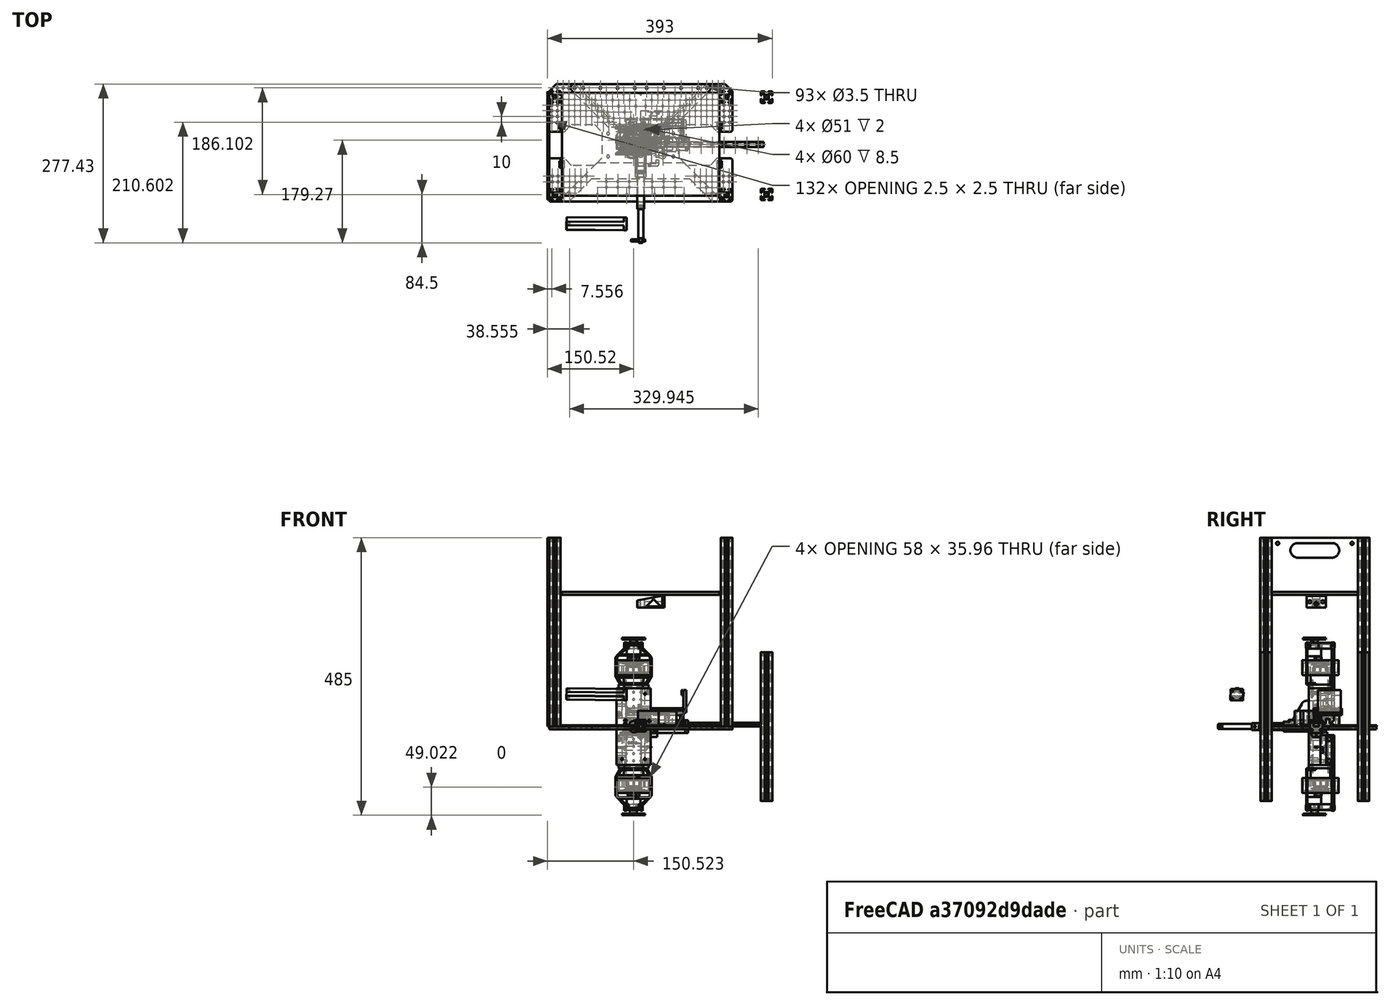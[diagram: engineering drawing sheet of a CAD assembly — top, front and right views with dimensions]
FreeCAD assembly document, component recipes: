
FREECAD ASSEMBLY — COMPONENT RECIPES ("NutSorter")

This assembly document has 31 components, labeled P0..P30 below (a component is one placed body or linked part). 29 of them carry a construction recipe — the FreeCAD feature program that regenerates the part from scratch, quoted from this document or its linked companion documents; the rest are supplied as boundary geometry only. No exploded tour is included for this assembly.
NOTE — this tour is split across 2 documents so each fits a 32k-token context. This is document 1: the component sections continue in the remaining 1 document, each repeating the header above.
COMPONENT P0 — recipe-attached ("support_pince_planche_bas", modeled in this document).
Construction recipe (the document's own serialized feature program — sketch geometry with constraints, then the solid features built on it; lengths are millimeters unless a unit is written):

FEATURE [Sketcher::SketchObject] Sketch042
  ArcFitTolerance = 1e-06
  AttachmentSupport = -> [XY_Plane019]
  FullyConstrained = true
  MakeInternals = false
  MapMode = 5
  Placement = pos=(0,0,0) rot=(0,1,0;3.14159rad)
  expr: Constraints[36] = 20 mm + VarSet.jeu
  expr: Constraints[37] = 40 mm + VarSet.jeu
  expr: Constraints[72] = 18 mm + VarSet.jeu
  expr: Constraints[73] = 20 mm + VarSet.jeu
  expr: Constraints[86] = 9 mm + VarSet.jeu
  expr: Constraints[87] = 6.5 mm + VarSet.jeu
  sketch-geometry (52):
    g0: LineSegment StartX=-28.5 StartY=-38 StartZ=0 EndX=1.8 EndY=-38 EndZ=0
    g1: LineSegment StartX=4.8 StartY=-35 StartZ=0 EndX=4.8 EndY=10 EndZ=0
    g2: ArcOfCircle CenterX=1.8 CenterY=-35 CenterZ=0 NormalX=0 NormalY=0 NormalZ=1 AngleXU=0 Radius=3 StartAngle=4.71239 EndAngle=6.28319
    g3: ArcOfCircle CenterX=1.8 CenterY=10 CenterZ=0 NormalX=0 NormalY=0 NormalZ=1 AngleXU=0 Radius=3 StartAngle=0 EndAngle=1.5708
    g4: GeomPoint [constr] X=4.8 Y=-38 Z=0
    g5: LineSegment StartX=-59.5 StartY=-13 StartZ=0 EndX=-34.5 EndY=-13 EndZ=0
    g6: LineSegment StartX=1.8 StartY=13 StartZ=0 EndX=-59.5 EndY=13 EndZ=0
    g7: ArcOfCircle CenterX=-59.5 CenterY=10 CenterZ=0 NormalX=0 NormalY=0 NormalZ=1 AngleXU=0 Radius=3 StartAngle=1.5708 EndAngle=3.14159
    g8: ArcOfCircle CenterX=-59.5 CenterY=-10 CenterZ=0 NormalX=0 NormalY=0 NormalZ=1 AngleXU=0 Radius=3 StartAngle=3.14159 EndAngle=4.71239
    g9: LineSegment StartX=-54.575 StartY=-10.075 StartZ=0 EndX=-16.425 EndY=-10.075 EndZ=0
    g10: LineSegment StartX=-15.425 StartY=-9.075 StartZ=0 EndX=-15.425 EndY=9.075 EndZ=0
    g11: LineSegment StartX=-16.425 StartY=10.075 StartZ=0 EndX=-54.575 EndY=10.075 EndZ=0
    g12: ArcOfCircle CenterX=-54.575 CenterY=9.075 CenterZ=0 NormalX=0 NormalY=0 NormalZ=1 AngleXU=0 Radius=1 StartAngle=1.5708 EndAngle=3.14159
    g13: ArcOfCircle CenterX=-54.575 CenterY=-9.075 CenterZ=0 NormalX=0 NormalY=0 NormalZ=1 AngleXU=0 Radius=1 StartAngle=3.14159 EndAngle=4.71239
    g14: ArcOfCircle CenterX=-16.425 CenterY=-9.075 CenterZ=0 NormalX=0 NormalY=0 NormalZ=1 AngleXU=0 Radius=1 StartAngle=4.71239 EndAngle=6.28319
    g15: ArcOfCircle CenterX=-16.425 CenterY=9.075 CenterZ=0 NormalX=0 NormalY=0 NormalZ=1 AngleXU=0 Radius=1 StartAngle=0 EndAngle=1.5708
    g16: GeomPoint [constr] X=-55.575 Y=10.075 Z=0
    g17: GeomPoint [constr] X=-15.425 Y=-10.075 Z=0
    g18: GeomPoint X=-35.5 Y=0 Z=0
    g19: ArcOfCircle CenterX=-34.5 CenterY=-16 CenterZ=0 NormalX=0 NormalY=0 NormalZ=1 AngleXU=0 Radius=3 StartAngle=0 EndAngle=1.5708
    g20: LineSegment StartX=-31.5 StartY=-16 StartZ=0 EndX=-31.5 EndY=-22.5 EndZ=0
    g21: ArcOfCircle CenterX=-28.5 CenterY=-35 CenterZ=0 NormalX=0 NormalY=0 NormalZ=1 AngleXU=0 Radius=3 StartAngle=3.14159 EndAngle=4.71239
    g22: GeomPoint [constr] X=-31.5 Y=-38 Z=0
    g23: GeomPoint X=-16.5 Y=-25 Z=0
    g24: LineSegment StartX=-26.575 StartY=-17.125 StartZ=0 EndX=-26.575 EndY=-22.5 EndZ=0
    g25: LineSegment StartX=-25.375 StartY=-34.075 StartZ=0 EndX=-7.625 EndY=-34.075 EndZ=0
    g26: LineSegment StartX=-6.425 StartY=-32.875 StartZ=0 EndX=-6.425 EndY=-17.125 EndZ=0
    g27: LineSegment StartX=-7.625 StartY=-15.925 StartZ=0 EndX=-25.375 EndY=-15.925 EndZ=0
    g28: ArcOfCircle CenterX=-25.375 CenterY=-17.125 CenterZ=0 NormalX=0 NormalY=0 NormalZ=1 AngleXU=0 Radius=1.2 StartAngle=1.5708 EndAngle=3.14159
    g29: ArcOfCircle CenterX=-25.375 CenterY=-32.875 CenterZ=0 NormalX=0 NormalY=0 NormalZ=1 AngleXU=0 Radius=1.2 StartAngle=3.14159 EndAngle=4.71239
    g30: ArcOfCircle CenterX=-7.625 CenterY=-32.875 CenterZ=0 NormalX=0 NormalY=0 NormalZ=1 AngleXU=0 Radius=1.2 StartAngle=4.71239 EndAngle=6.28319
    g31: ArcOfCircle CenterX=-7.625 CenterY=-17.125 CenterZ=0 NormalX=0 NormalY=0 NormalZ=1 AngleXU=0 Radius=1.2 StartAngle=-9e-16 EndAngle=1.5708
    g32: GeomPoint [constr] X=-26.575 Y=-15.925 Z=0
    g33: GeomPoint [constr] X=-6.425 Y=-34.075 Z=0
    g34: LineSegment StartX=-6.575 StartY=4.575 StartZ=0 EndX=-6.575 EndY=-4.575 EndZ=0
    g35: LineSegment StartX=-6.575 StartY=-4.575 StartZ=0 EndX=0.075 EndY=-4.575 EndZ=0
    g36: LineSegment StartX=0.075 StartY=-4.575 StartZ=0 EndX=0.075 EndY=4.575 EndZ=0
    g37: LineSegment StartX=0.075 StartY=4.575 StartZ=0 EndX=-6.575 EndY=4.575 EndZ=0
    g38: GeomPoint X=-3.25 Y=0 Z=0
    g39: LineSegment StartX=-26.575 StartY=-22.5 StartZ=0 EndX=-31.5 EndY=-22.5 EndZ=0
    g40: LineSegment StartX=-31.5 StartY=-27.5 StartZ=0 EndX=-26.575 EndY=-27.5 EndZ=0
    g41: LineSegment StartX=-26.575 StartY=-27.5 StartZ=0 EndX=-26.575 EndY=-32.875 EndZ=0
    g42: LineSegment StartX=-31.5 StartY=-27.5 StartZ=0 EndX=-31.5 EndY=-35 EndZ=0
    g43: LineSegment [constr] StartX=-16.5 StartY=-25 StartZ=0 EndX=-31.5 EndY=-25 EndZ=0
    g44: LineSegment StartX=-62.5 StartY=4 StartZ=0 EndX=-55.575 EndY=4 EndZ=0
    g45: LineSegment StartX=-62.5 StartY=-4 StartZ=0 EndX=-55.575 EndY=-4 EndZ=0
    g46: LineSegment StartX=-55.575 StartY=-4 StartZ=0 EndX=-55.575 EndY=-9.075 EndZ=0
    g47: LineSegment StartX=-62.5 StartY=-4 StartZ=0 EndX=-62.5 EndY=-10 EndZ=0
    g48: LineSegment StartX=-62.5 StartY=10 StartZ=0 EndX=-62.5 EndY=4 EndZ=0
    g49: LineSegment StartX=-55.575 StartY=9.075 StartZ=0 EndX=-55.575 EndY=4 EndZ=0
    g50: Circle CenterX=-10.5 CenterY=6 CenterZ=0 NormalX=0 NormalY=0 NormalZ=1 AngleXU=0 Radius=1.75
    g51: Circle CenterX=-10.5 CenterY=-6 CenterZ=0 NormalX=0 NormalY=0 NormalZ=1 AngleXU=0 Radius=1.75
  constraints (130):
    c: Tangent(g0,g2) = -1.5708
    c: Tangent(g1,g2) = -1.5708
    c: Tangent(g1,g3) = -1.5708
    c: Vertical(g1)
    c: Horizontal(g0)
    c: Equal(g2,g3)
    c: PointOnObject(g4,g0)
    c: PointOnObject(g4,g1)
    c: DistanceX(g-1,g1) = 4.8
    c: Tangent(g5,g8) = -1.5708
    c: Tangent(g6,g7) = -1.5708
    c: Horizontal(g5)
    c: Horizontal(g6)
    c: Equal(g7,g8)
    c: DistanceY(g5,g6) = 26
    c: Symmetric(g7,g47,g-1)
    c: Radius(g7) = 3
    c: Tangent(g3,g6) = -1.5708
    c: Tangent(g9,g13) = -1.5708
    c: Tangent(g9,g14) = -1.5708
    c: Tangent(g10,g14) = -1.5708
    c: Tangent(g10,g15) = -1.5708
    c: Tangent(g11,g15) = -1.5708
    c: Tangent(g11,g12) = -1.5708
    c: Vertical(g10)
    c: Horizontal(g9)
    c: Horizontal(g11)
    c: Equal(g12,g13)
    c: Equal(g13,g14)
    c: Equal(g14,g15)
    c: PointOnObject(g16,g11)
    c: PointOnObject(g17,g9)
    c: PointOnObject(g17,g10)
    c: Radius(g13) = 1
    c: PointOnObject(g18,g-1)
    c: Symmetric(g16,g17,g18)
    c: DistanceY(g9,g11) = 20.15
    c: DistanceX(g12,g10) = 40.15
    c: DistanceX(g18,g-1) = 35.5
    c: DistanceX(g7,g18) = 27
    c: Vertical(g20)
    c: PointOnObject(g22,g42)
    c: PointOnObject(g22,g0)
    c: Tangent(g0,g21) = -1.5708
    c: Tangent(g19,g5) = 1.5708
    c: Tangent(g20,g19) = 1.5708
    c: DistanceY(g23,g-1) = 25
    c: DistanceX(g23,g-1) = 16.5
    c: DistanceX(g19,g23) = 15
    c: DistanceY(g0,g23) = 13
    c: Equal(g21,g19)
    c: Equal(g19,g2)
    c: Equal(g3,g7)
    c: Tangent(g24,g28) = -1.5708
    c: Tangent(g25,g29) = -1.5708
    c: Tangent(g25,g30) = -1.5708
    c: Tangent(g26,g30) = -1.5708
    c: Tangent(g26,g31) = -1.5708
    c: Tangent(g27,g31) = -1.5708
    c: Tangent(g27,g28) = -1.5708
    c: Vertical(g24)
    c: Vertical(g26)
    c: Horizontal(g25)
    c: Horizontal(g27)
    c: Equal(g28,g29)
    c: Equal(g29,g30)
    c: Equal(g30,g31)
    c: PointOnObject(g32,g24)
    c: PointOnObject(g32,g27)
    c: PointOnObject(g33,g25)
    c: PointOnObject(g33,g26)
    c: Symmetric(g33,g32,g23)
    c: DistanceY(g25,g27) = 18.15
    c: DistanceX(g24,g26) = 20.15
    c: Radius(g31) = 1.2
    c: Coincident(g34,g35)
    c: Coincident(g35,g36)
    c: Coincident(g36,g37)
    c: Coincident(g37,g34)
    c: Vertical(g34)
    c: Vertical(g36)
    c: Horizontal(g35)
    c: Horizontal(g37)
    c: PointOnObject(g38,g-1)
    c: Symmetric(g36,g34,g38)
    c: DistanceX(g38,g-1) = 3.25
    c: DistanceY(g34,g34) = 9.15
    c: DistanceX(g37,g37) = 6.65
    c: Horizontal(g39)
    c: Horizontal(g40)
    c: PointOnObject(g40,g41)
    c: PointOnObject(g40,g42)
    c: Coincident(g24,g39)
    c: PointOnObject(g41,g40)
    c: Coincident(g20,g39)
    c: PointOnObject(g42,g40)
    c: Coincident(g43,g23)
    c: Horizontal(g43)
    c: Symmetric(g20,g40,g43)
    c: Vertical(g24,g40)
    c: Vertical(g40,g20)
    c: DistanceY(g40,g24) = 5
    c: Vertical(g41)
    c: Tangent(g41,g29) = -1.5708
    c: Tangent(g42,g21) = -1.5708
    c: Vertical(g42)
    c: Horizontal(g44)
    c: PointOnObject(g45,g47)
    c: Horizontal(g45)
    c: PointOnObject(g45,g46)
    c: PointOnObject(g46,g45)
    c: PointOnObject(g47,g45)
    c: Coincident(g48,g44)
    c: Vertical(g48)
    c: Tangent(g7,g48) = -1.5708
    c: Tangent(g47,g8) = -1.5708
    c: Tangent(g46,g13) = -1.5708
    c: Vertical(g46)
    c: Vertical(g47)
    c: Coincident(g49,g44)
    c: Vertical(g49)
    c: Tangent(g49,g12) = -1.5708
    c: Symmetric(g44,g45,g-1)
    c: Vertical(g16,g12)
    c: DistanceY(g45,g44) = 8
    c: Symmetric(g50,g51,g-1)
    c: DistanceX(g18,g51) = 25
    c: DistanceY(g18,g50) = 6
    c: Equal(g50,g51)
    c: Diameter(g50) = 3.5
FEATURE [PartDesign::Pad] Pad015
  Direction = (0,0,-1)
  Length = 27.5
  Length2 = 10
  Profile = -> Sketch042
  ReferenceAxis = -> Sketch042 [N_Axis]
  Reversed = true
  Suppressed = false
  Type = 0
FEATURE [Sketcher::SketchObject] Sketch055
  ArcFitTolerance = 1e-06
  AttachmentSupport = -> [XY_Plane019]
  ExternalGeometry = -> [Pad015]
  FullyConstrained = true
  MakeInternals = false
  MapMode = 5
  Placement = pos=(0,0,0) rot=(0,1,0;3.14159rad)
  sketch-geometry (8):
    g0: LineSegment StartX=-6.575 StartY=4.575 StartZ=0 EndX=-6.575 EndY=-4.575 EndZ=0
    g1: LineSegment StartX=-6.575 StartY=-4.575 StartZ=0 EndX=0.075 EndY=-4.575 EndZ=0
    g2: LineSegment StartX=0.075 StartY=-4.575 StartZ=0 EndX=0.075 EndY=4.575 EndZ=0
    g3: LineSegment StartX=0.075 StartY=4.575 StartZ=0 EndX=-6.575 EndY=4.575 EndZ=0
    g4: LineSegment StartX=-18.425 StartY=-15.925 StartZ=0 EndX=-18.425 EndY=-34.075 EndZ=0
    g5: LineSegment StartX=-18.425 StartY=-34.075 StartZ=0 EndX=-6.425 EndY=-34.075 EndZ=0
    g6: LineSegment StartX=-6.425 StartY=-34.075 StartZ=0 EndX=-6.425 EndY=-15.925 EndZ=0
    g7: LineSegment StartX=-6.425 StartY=-15.925 StartZ=0 EndX=-18.425 EndY=-15.925 EndZ=0
  constraints (22):
    c: Coincident(g0,g1)
    c: Coincident(g1,g2)
    c: Coincident(g2,g3)
    c: Coincident(g3,g0)
    c: Vertical(g0)
    c: Vertical(g2)
    c: Horizontal(g1)
    c: Horizontal(g3)
    c: Coincident(g4,g5)
    c: Coincident(g5,g6)
    c: Coincident(g6,g7)
    c: Coincident(g7,g4)
    c: Vertical(g4)
    c: Vertical(g6)
    c: Horizontal(g5)
    c: Horizontal(g7)
    c: PointOnObject(g4,g-5)
    c: PointOnObject(g6,g-6)
    c: PointOnObject(g5,g-7)
    c: DistanceX(g7,g7) = 12
    c: Coincident(g0,g-3)
    c: Coincident(g1,g-4)
FEATURE [PartDesign::Pad] Pad023
  BaseFeature = -> Pad015
  Direction = (0,0,-1)
  Length = 5
  Length2 = 10
  Profile = -> Sketch055
  ReferenceAxis = -> Sketch055 [N_Axis]
  Reversed = true
  Suppressed = false
  Type = 0
FEATURE [Sketcher::SketchObject] Sketch056
  ArcFitTolerance = 1e-06
  AttachmentOffset = pos=(0,0,-0.25) rot=(0,0,1;0rad)
  AttachmentSupport = -> [YZ_Plane019]
  ExternalGeometry = -> [Pad023]
  FullyConstrained = true
  MakeInternals = false
  MapMode = 5
  Placement = pos=(-0.25,0,0) rot=(0.57735,0.57735,0.57735;2.0944rad)
  sketch-geometry (7):
    g0: LineSegment StartX=-8.575 StartY=27.5 StartZ=0 EndX=8.575 EndY=27.5 EndZ=0
    g1: LineSegment StartX=4.575 StartY=31.5 StartZ=0 EndX=4.575 EndY=34.5 EndZ=0
    g2: LineSegment StartX=-4.575 StartY=34.5 StartZ=0 EndX=-4.575 EndY=31.5 EndZ=0
    g3: ArcOfCircle CenterX=0 CenterY=34.5 CenterZ=0 NormalX=0 NormalY=0 NormalZ=1 AngleXU=0 Radius=4.575 StartAngle=0 EndAngle=3.14159
    g4: Circle CenterX=0 CenterY=34.5 CenterZ=0 NormalX=0 NormalY=0 NormalZ=1 AngleXU=0 Radius=1.75
    g5: ArcOfCircle CenterX=-8.575 CenterY=31.5 CenterZ=0 NormalX=0 NormalY=0 NormalZ=1 AngleXU=0 Radius=4 StartAngle=4.71239 EndAngle=6.28319
    g6: ArcOfCircle CenterX=8.575 CenterY=31.5 CenterZ=0 NormalX=0 NormalY=0 NormalZ=1 AngleXU=0 Radius=4 StartAngle=3.14159 EndAngle=4.71239
  constraints (17):
    c: Vertical(g1)
    c: Vertical(g2)
    c: PointOnObject(g3,g-2)
    c: DistanceY(g-1,g3) = 34.5
    c: Tangent(g3,g1) = -1.5708
    c: Coincident(g4,g3)
    c: Diameter(g4) = 3.5
    c: Tangent(g3,g2) = -1.5708
    c: Tangent(g2,g5) = 1.5708
    c: Tangent(g0,g5) = -1.5708
    c: Horizontal(g0,g-3)
    c: Vertical(g2,g-3)
    c: Horizontal(g0,g-3)
    c: Tangent(g6,g1) = 1.5708
    c: Tangent(g0,g6) = -1.5708
    c: Equal(g1,g2)
    c: Radius(g6) = 4
FEATURE [PartDesign::Pad] Pad024
  BaseFeature = -> Pad023
  Direction = (1,0,0)
  Length = 4
  Length2 = 10
  Profile = -> Sketch056
  ReferenceAxis = -> Sketch056 [N_Axis]
  Reversed = true
  Suppressed = false
  Type = 0
FEATURE [Sketcher::SketchObject] Sketch057
  ArcFitTolerance = 1e-06
  AttachmentSupport = -> [XY_Plane019]
  ExternalGeometry = -> [Pad024]
  FullyConstrained = true
  MakeInternals = false
  MapMode = 5
  sketch-geometry (14):
    g0: ArcOfCircle CenterX=34.5 CenterY=-16 CenterZ=0 NormalX=0 NormalY=0 NormalZ=1 AngleXU=0 Radius=3 StartAngle=1.5708 EndAngle=3.14159
    g1: ArcOfCircle CenterX=39 CenterY=-20 CenterZ=0 NormalX=0 NormalY=0 NormalZ=1 AngleXU=0 Radius=5 StartAngle=4.34942 EndAngle=6.76197
    g2: LineSegment StartX=31.5 StartY=-16 StartZ=0 EndX=31.5 EndY=-22.5 EndZ=0
    g3: LineSegment StartX=34.5 StartY=-13 StartZ=0 EndX=41 EndY=-13 EndZ=0
    g4: Circle CenterX=39 CenterY=-20 CenterZ=0 NormalX=0 NormalY=0 NormalZ=1 AngleXU=0 Radius=1.75
    g5: LineSegment StartX=31.5 StartY=-22.5 StartZ=0 EndX=37.2247 EndY=-24.6742 EndZ=0
    g6: LineSegment StartX=43.4378 StartY=-17.6965 StartZ=0 EndX=41 EndY=-13 EndZ=0
    g7: Circle CenterX=29.2 CenterY=20 CenterZ=0 NormalX=0 NormalY=0 NormalZ=1 AngleXU=0 Radius=1.75
    g8: LineSegment StartX=20.2 StartY=13 StartZ=0 EndX=38.2 EndY=13 EndZ=0
    g9: LineSegment StartX=34.2 StartY=17 StartZ=0 EndX=34.2 EndY=20 EndZ=0
    g10: LineSegment StartX=24.2 StartY=17 StartZ=0 EndX=24.2 EndY=20 EndZ=0
    g11: ArcOfCircle CenterX=29.2 CenterY=20 CenterZ=0 NormalX=0 NormalY=0 NormalZ=1 AngleXU=0 Radius=5 StartAngle=0 EndAngle=3.14159
    g12: ArcOfCircle CenterX=20.2 CenterY=17 CenterZ=0 NormalX=0 NormalY=0 NormalZ=1 AngleXU=0 Radius=4 StartAngle=4.71239 EndAngle=6.28319
    g13: ArcOfCircle CenterX=38.2 CenterY=17 CenterZ=0 NormalX=0 NormalY=0 NormalZ=1 AngleXU=0 Radius=4 StartAngle=3.14159 EndAngle=4.71239
  constraints (34):
    c: Coincident(g0,g-3)
    c: Coincident(g3,g0)
    c: Horizontal(g3)
    c: Vertical(g2)
    c: Tangent(g2,g0) = -1.5708
    c: Coincident(g0,g-3)
    c: Coincident(g4,g1)
    c: Diameter(g4) = 3.5
    c: Radius(g1) = 5
    c: Coincident(g2,g5)
    c: Tangent(g5,g1) = -1.5708
    c: Coincident(g6,g3)
    c: Tangent(g6,g1) = -1.5708
    c: Equal(g3,g2)
    c: DistanceX(g3,g3) = 6.5
    c: Horizontal(g8)
    c: Vertical(g9)
    c: Vertical(g10)
    c: PointOnObject(g8,g-4)
    c: Coincident(g7,g11)
    c: Tangent(g11,g9) = -1.5708
    c: Tangent(g11,g10) = 1.5708
    c: Tangent(g10,g12) = -1.5708
    c: Tangent(g8,g12) = -1.5708
    c: Tangent(g13,g9) = 1.5708
    c: Tangent(g13,g8) = -1.5708
    c: Diameter(g7) = 3.5
    c: Equal(g11,g1)
    c: Equal(g10,g9)
    c: Radius(g13) = 4
    c: DistanceY(g-1,g7) = 20
    c: DistanceX(g-1,g7) = 29.2
    c: DistanceY(g1,g-1) = 20
    c: DistanceX(g-1,g1) = 39
FEATURE [PartDesign::Pad] Pad025
  BaseFeature = -> Pad024
  Direction = (0,0,1)
  Length = 3
  Length2 = 10
  Profile = -> Sketch057
  ReferenceAxis = -> Sketch057 [N_Axis]
  Suppressed = false
  Type = 0
FEATURE [Sketcher::SketchObject] Sketch058
  ArcFitTolerance = 1e-06
  AttachmentOffset = pos=(15,9.6,25) rot=(0,0,1;0rad)
  AttachmentSupport = -> [XZ_Plane019]
  FullyConstrained = true
  MakeInternals = false
  MapMode = 5
  Placement = pos=(15,-25,9.6) rot=(1,0,0;1.5708rad)
  sketch-geometry (2):
    g0: ArcOfCircle CenterX=0 CenterY=0 CenterZ=0 NormalX=0 NormalY=0 NormalZ=1 AngleXU=0 Radius=2.25 StartAngle=1.99427 EndAngle=7.43051
    g1: ArcOfCircle CenterX=0 CenterY=1 CenterZ=0 NormalX=0 NormalY=0 NormalZ=1 AngleXU=0 Radius=1.4 StartAngle=0.849413 EndAngle=2.29218
  constraints (7):
    c: Coincident(g0,g-1)
    c: Diameter(g0) = 4.5
    c: Coincident(g1,g0)
    c: Coincident(g1,g0)
    c: PointOnObject(g1,g-2)
    c: DistanceY(g0,g1) = 1
    c: Radius(g1) = 1.4
FEATURE [PartDesign::Pocket] Pocket028
  BaseFeature = -> Pad025
  Direction = (0,1,-2e-16)
  Length = 27
  Length2 = 5
  Midplane = true
  Profile = -> Sketch058
  ReferenceAxis = -> Sketch058 [N_Axis]
  Suppressed = false
  Type = 0
FEATURE [Sketcher::SketchObject] Sketch059
  ArcFitTolerance = 1e-06
  AttachmentSupport = -> [Pocket028]
  ExternalGeometry = -> [Pocket028]
  FullyConstrained = true
  MakeInternals = false
  MapMode = 5
  Placement = pos=(0,0,27.5) rot=(0,0,1;0rad)
  sketch-geometry (2):
    g0: Circle CenterX=10.5 CenterY=6 CenterZ=0 NormalX=0 NormalY=0 NormalZ=1 AngleXU=0 Radius=2.1
    g1: Circle CenterX=10.5 CenterY=-6 CenterZ=0 NormalX=0 NormalY=0 NormalZ=1 AngleXU=0 Radius=2.1
  constraints (4):
    c: Coincident(g0,g-3)
    c: Coincident(g1,g-4)
    c: Equal(g0,g1)
    c: Diameter(g0) = 4.2
FEATURE [PartDesign::Pocket] Pocket029
  BaseFeature = -> Pocket028
  Direction = (0,0,-1)
  Length = 1.5
  Length2 = 5
  Profile = -> Sketch059
  ReferenceAxis = -> Sketch059 [N_Axis]
  Suppressed = false
  Type = 0
FEATURE [PartDesign::Fillet] Fillet
  Base = -> Pocket029 [Edge169,Edge108]
  BaseFeature = -> Pocket029
  Radius = 3
  SupportTransform = false
  Suppressed = false
  UseAllEdges = false
FEATURE [PartDesign::Body] Body013  label="support_pince_planche_bas"
  AllowCompound = false
  Group = -> [Sketch042,Pad015,Sketch055,Pad023,Sketch056,Pad024,Sketch057,Pad025,Sketch058,Pocket028,Sketch059,Pocket029,Fillet]
  Origin = -> Origin019
  Tip = -> Fillet
COMPONENT P1 — recipe-attached ("support_pince_planche_haut", modeled in this document).
Construction recipe (the document's own serialized feature program — sketch geometry with constraints, then the solid features built on it; lengths are millimeters unless a unit is written):

FEATURE [Sketcher::SketchObject] Sketch063
  ArcFitTolerance = 1e-06
  AttachmentSupport = -> [XY_Plane024]
  FullyConstrained = true
  MakeInternals = false
  MapMode = 5
  sketch-geometry (11):
    g0: LineSegment StartX=-3.15 StartY=4.65 StartZ=0 EndX=-3.15 EndY=-4.65 EndZ=0
    g1: LineSegment StartX=-3.15 StartY=-4.65 StartZ=0 EndX=3.15 EndY=-4.65 EndZ=0
    g2: LineSegment StartX=3.15 StartY=-4.65 StartZ=0 EndX=3.15 EndY=4.65 EndZ=0
    g3: LineSegment StartX=3.15 StartY=4.65 StartZ=0 EndX=-3.15 EndY=4.65 EndZ=0
    g4: LineSegment StartX=-6.15 StartY=4.65 StartZ=0 EndX=-6.15 EndY=-4.65 EndZ=0
    g5: LineSegment StartX=-3.15 StartY=-7.65 StartZ=0 EndX=38.5 EndY=-7.65 EndZ=0
    g6: LineSegment StartX=38.5 StartY=-7.65 StartZ=0 EndX=38.5 EndY=7.65 EndZ=0
    g7: LineSegment StartX=38.5 StartY=7.65 StartZ=0 EndX=-3.15 EndY=7.65 EndZ=0
    g8: ArcOfCircle CenterX=-3.15 CenterY=4.65 CenterZ=0 NormalX=0 NormalY=0 NormalZ=1 AngleXU=0 Radius=3 StartAngle=1.5708 EndAngle=3.14159
    g9: ArcOfCircle CenterX=-3.15 CenterY=-4.65 CenterZ=0 NormalX=0 NormalY=0 NormalZ=1 AngleXU=0 Radius=3 StartAngle=3.14159 EndAngle=4.71239
    g10: GeomPoint [constr] X=-6.15 Y=7.65 Z=0
  constraints (27):
    c: Coincident(g0,g1)
    c: Coincident(g1,g2)
    c: Coincident(g2,g3)
    c: Coincident(g3,g0)
    c: Vertical(g0)
    c: Vertical(g2)
    c: Horizontal(g1)
    c: Horizontal(g3)
    c: Tangent(g4,g8) = -1.5708
    c: Tangent(g4,g9) = -1.5708
    c: Tangent(g5,g9) = -1.5708
    c: Tangent(g7,g8) = -1.5708
    c: Vertical(g4)
    c: Horizontal(g5)
    c: Horizontal(g7)
    c: Equal(g8,g9)
    c: PointOnObject(g10,g4)
    c: PointOnObject(g10,g7)
    c: Radius(g9) = 3
    c: Coincident(g6,g7)
    c: Coincident(g5,g6)
    c: Symmetric(g6,g5,g-1)
    c: Symmetric(g2,g0,g-1)
    c: DistanceY(g0,g0) = 9.3
    c: DistanceX(g3,g3) = 6.3
    c: Coincident(g0,g8)
    c: DistanceX(g-1,g6) = 38.5
FEATURE [PartDesign::Pad] Pad029
  Direction = (0,0,1)
  Length = 5
  Length2 = 10
  Profile = -> Sketch063
  ReferenceAxis = -> Sketch063 [N_Axis]
  Suppressed = false
  Type = 0
FEATURE [Sketcher::SketchObject] Sketch064
  ArcFitTolerance = 1e-06
  AttachmentSupport = -> [Pad029]
  ExternalGeometry = -> [Pad029]
  FullyConstrained = true
  MakeInternals = false
  MapMode = 5
  Placement = pos=(38.5,0,0) rot=(0.57735,0.57735,0.57735;2.0944rad)
  sketch-geometry (8):
    g0: Circle CenterX=0 CenterY=16 CenterZ=0 NormalX=0 NormalY=0 NormalZ=1 AngleXU=0 Radius=2.75
    g1: LineSegment StartX=-7.65 StartY=19 StartZ=0 EndX=-7.65 EndY=5 EndZ=0
    g2: LineSegment StartX=7.65 StartY=5 StartZ=0 EndX=7.65 EndY=19 EndZ=0
    g3: LineSegment StartX=4.65 StartY=22 StartZ=0 EndX=-4.65 EndY=22 EndZ=0
    g4: ArcOfCircle CenterX=-4.65 CenterY=19 CenterZ=0 NormalX=0 NormalY=0 NormalZ=1 AngleXU=0 Radius=3 StartAngle=1.5708 EndAngle=3.14159
    g5: ArcOfCircle CenterX=4.65 CenterY=19 CenterZ=0 NormalX=0 NormalY=0 NormalZ=1 AngleXU=0 Radius=3 StartAngle=-9e-16 EndAngle=1.5708
    g6: GeomPoint [constr] X=-7.65 Y=22 Z=0
    g7: LineSegment StartX=-7.65 StartY=5 StartZ=0 EndX=7.65 EndY=5 EndZ=0
  constraints (19):
    c: Diameter(g0) = 5.5
    c: PointOnObject(g0,g-2)
    c: Tangent(g1,g4) = -1.5708
    c: Tangent(g2,g5) = -1.5708
    c: Tangent(g3,g5) = -1.5708
    c: Tangent(g3,g4) = -1.5708
    c: Vertical(g1)
    c: Vertical(g2)
    c: Horizontal(g3)
    c: PointOnObject(g6,g1)
    c: PointOnObject(g6,g3)
    c: Coincident(g1,g-3)
    c: Coincident(g2,g-3)
    c: Equal(g5,g4)
    c: Radius(g4) = 3
    c: DistanceY(g2,g0) = 11
    c: Coincident(g7,g1)
    c: Coincident(g7,g2)
    c: DistanceY(g0,g3) = 6
FEATURE [PartDesign::Pad] Pad030
  BaseFeature = -> Pad029
  Direction = (1,0,0)
  Length = 3
  Length2 = 10
  Profile = -> Sketch064
  ReferenceAxis = -> Sketch064 [N_Axis]
  Reversed = true
  Suppressed = false
  Type = 0
FEATURE [PartDesign::Chamfer] Chamfer  label="Chamfer001"
  Angle = 45
  Base = -> Pad030 [Edge19]
  BaseFeature = -> Pad030
  ChamferType = 1
  FlipDirection = false
  Size = 15
  Size2 = 5
  SupportTransform = false
  Suppressed = false
  UseAllEdges = false
FEATURE [PartDesign::Body] Body017  label="support_pince_planche_haut"
  AllowCompound = false
  Group = -> [Sketch063,Pad029,Sketch064,Pad030,Chamfer]
  Origin = -> Origin024
  Placement = pos=(3,-2.563e-05,214) rot=(0,0,1;0rad)
  Tip = -> Chamfer
COMPONENT P2 — recipe-attached ("pince_capot001", modeled in this document).
Construction recipe (the document's own serialized feature program — sketch geometry with constraints, then the solid features built on it; lengths are millimeters unless a unit is written):

FEATURE [Sketcher::SketchObject] Sketch242
  ArcFitTolerance = 0
  AttachmentSupport = -> [XY_Plane281]
  FullyConstrained = true
  MakeInternals = false
  MapMode = 2
  sketch-geometry (31):
    g0: LineSegment StartX=0 StartY=50 StartZ=0 EndX=100 EndY=50 EndZ=0
    g1: LineSegment StartX=100 StartY=50 StartZ=0 EndX=100 EndY=48 EndZ=0
    g2: LineSegment StartX=100 StartY=0 StartZ=0 EndX=0 EndY=0 EndZ=0
    g3: LineSegment StartX=0 StartY=0 StartZ=0 EndX=0 EndY=2 EndZ=0
    g4: Circle CenterX=50 CenterY=25 CenterZ=0 NormalX=0 NormalY=0 NormalZ=1 AngleXU=0 Radius=14
    g5: LineSegment [constr] StartX=0 StartY=50 StartZ=0 EndX=100 EndY=0 EndZ=0
    g6: LineSegment [constr] StartX=0 StartY=0 StartZ=0 EndX=100 EndY=50 EndZ=0
    g7: LineSegment [constr] StartX=0 StartY=25 StartZ=0 EndX=100 EndY=25 EndZ=0
    g8: LineSegment [constr] StartX=50 StartY=50 StartZ=0 EndX=50 EndY=0 EndZ=0
    g9: LineSegment [constr] StartX=3.5 StartY=33.25 StartZ=0 EndX=96.5 EndY=33.25 EndZ=0
    g10: LineSegment [constr] StartX=96.5 StartY=33.25 StartZ=0 EndX=96.5 EndY=16.75 EndZ=0
    g11: LineSegment [constr] StartX=96.5 StartY=16.75 StartZ=0 EndX=3.5 EndY=16.75 EndZ=0
    g12: LineSegment [constr] StartX=3.5 StartY=16.75 StartZ=0 EndX=3.5 EndY=33.25 EndZ=0
    g13: Circle CenterX=96.5 CenterY=33.25 CenterZ=0 NormalX=0 NormalY=0 NormalZ=1 AngleXU=0 Radius=1.65
    g14: Circle CenterX=3.5 CenterY=33.25 CenterZ=0 NormalX=0 NormalY=0 NormalZ=1 AngleXU=0 Radius=1.65
    g15: Circle CenterX=3.5 CenterY=16.75 CenterZ=0 NormalX=0 NormalY=0 NormalZ=1 AngleXU=0 Radius=1.65
    g16: Circle CenterX=96.5 CenterY=16.75 CenterZ=0 NormalX=0 NormalY=0 NormalZ=1 AngleXU=0 Radius=1.65
    g17: LineSegment StartX=0 StartY=2 StartZ=0 EndX=30 EndY=2 EndZ=0
    g18: LineSegment StartX=30 StartY=2 StartZ=0 EndX=30 EndY=7.5 EndZ=0
    g19: LineSegment StartX=30 StartY=7.5 StartZ=0 EndX=2.5 EndY=7.5 EndZ=0
    g20: LineSegment StartX=0 StartY=10 StartZ=0 EndX=0 EndY=50 EndZ=0
    g21: LineSegment StartX=100 StartY=48 StartZ=0 EndX=67.5 EndY=48 EndZ=0
    g22: LineSegment StartX=67.5 StartY=48 StartZ=0 EndX=67.5 EndY=42.5 EndZ=0
    g23: LineSegment StartX=67.5 StartY=42.5 StartZ=0 EndX=97.5 EndY=42.5 EndZ=0
    g24: LineSegment StartX=100 StartY=40 StartZ=0 EndX=100 EndY=0 EndZ=0
    g25: ArcOfCircle [constr] CenterX=97.5 CenterY=40 CenterZ=0 NormalX=0 NormalY=0 NormalZ=1 AngleXU=0 Radius=2.5 StartAngle=0 EndAngle=1.5708
    g26: GeomPoint [constr] X=100 Y=42.5 Z=0
    g27: LineSegment StartX=100 StartY=40 StartZ=0 EndX=97.5 EndY=42.5 EndZ=0
    g28: ArcOfCircle [constr] CenterX=2.5 CenterY=10 CenterZ=0 NormalX=0 NormalY=0 NormalZ=1 AngleXU=0 Radius=2.5 StartAngle=3.14159 EndAngle=4.71239
    g29: GeomPoint [constr] X=0 Y=7.5 Z=0
    g30: LineSegment StartX=0 StartY=10 StartZ=0 EndX=2.5 EndY=7.5 EndZ=0
  constraints (78):
    c: Coincident(g0,g1)
    c: Coincident(g24,g2)
    c: Coincident(g2,g3)
    c: Coincident(g20,g0)
    c: Horizontal(g0)
    c: Horizontal(g2)
    c: Vertical(g1)
    c: Vertical(g3)
    c: Coincident(g2,g-1)
    c: Coincident(g5,g0)
    c: Coincident(g2,g6)
    c: Coincident(g0,g6)
    c: Coincident(g24,g5)
    c: PointOnObject(g4,g6)
    c: PointOnObject(g4,g5)
    c: Diameter(g4) = 28
    c: DistanceY(g3,g20) = 50
    c: DistanceX(g2,g2) = 100
    c: PointOnObject(g8,g0)
    c: PointOnObject(g7,g24)
    c: PointOnObject(g7,g20)
    c: PointOnObject(g8,g2)
    c: Symmetric(g0,g0,g8)
    c: Symmetric(g0,g2,g7)
    c: Coincident(g9,g10)
    c: Coincident(g10,g11)
    c: Coincident(g11,g12)
    c: Coincident(g12,g9)
    c: Horizontal(g11)
    c: Vertical(g12)
    c: Symmetric(g9,g10,g7)
    c: Symmetric(g9,g9,g8)
    c: Distance(g12) = 16.5
    c: DistanceX(g0,g9) = 3.5
    c: Coincident(g16,g10)
    c: Coincident(g13,g9)
    c: Coincident(g9,g14)
    c: Coincident(g11,g15)
    c: Equal(g14,g15)
    c: Equal(g14,g13)
    c: Equal(g14,g16)
    c: Diameter(g14) = 3.3
    c: Coincident(g17,g18)
    c: Coincident(g18,g19)
    c: Horizontal(g17)
    c: Horizontal(g19)
    c: Vertical(g18)
    c: Vertical(g20)
    c: DistanceX(g29,g19) = 30
    c: Coincident(g21,g22)
    c: Coincident(g22,g23)
    c: Horizontal(g21)
    c: Horizontal(g23)
    c: Vertical(g22)
    c: Vertical(g24)
    c: Equal(g18,g22)
    c: PointOnObject(g26,g23)
    c: PointOnObject(g26,g24)
    c: Tangent(g23,g25) = 1.5708
    c: Tangent(g24,g25) = 1.5708
    c: Coincident(g27,g23)
    c: Coincident(g27,g24)
    c: PointOnObject(g29,g20)
    c: PointOnObject(g29,g19)
    c: Tangent(g20,g28) = 1.5708
    c: Tangent(g19,g28) = 1.5708
    c: Coincident(g30,g20)
    c: Coincident(g30,g19)
    c: Equal(g1,g3)
    c: Equal(g23,g17)
    c: Coincident(g3,g17)
    c: DistanceY(g3,g3) = 2
    c: Coincident(g1,g21)
    c: Vertical(g1,g24)
    c: Vertical(g29,g3)
    c: DistanceY(g18,g18) = 5.5
    c: Radius(g28) = 2.5
    c: Equal(g25,g28)
FEATURE [PartDesign::Pad] Pad118
  AlongSketchNormal = false
  Direction = (0,0,1)
  Length = 4
  Length2 = 100
  Profile = -> Sketch242
  ReferenceAxis = -> Sketch242 [N_Axis]
  Suppressed = false
  Type = 0
FEATURE [Sketcher::SketchObject] Sketch243
  ArcFitTolerance = 1e-06
  AttachmentOffset = pos=(0,0,4) rot=(0,0,1;0rad)
  AttachmentSupport = -> [XY_Plane281]
  ExternalGeometry = -> [Pad118]
  FullyConstrained = true
  MakeInternals = false
  MapMode = 5
  Placement = pos=(0,0,4) rot=(0,0,1;0rad)
  sketch-geometry (4):
    g0: Circle CenterX=3.5 CenterY=33.25 CenterZ=0 NormalX=0 NormalY=0 NormalZ=1 AngleXU=0 Radius=3.25
    g1: Circle CenterX=3.5 CenterY=16.75 CenterZ=0 NormalX=0 NormalY=0 NormalZ=1 AngleXU=0 Radius=3.25
    g2: Circle CenterX=96.5 CenterY=33.25 CenterZ=0 NormalX=0 NormalY=0 NormalZ=1 AngleXU=0 Radius=3.25
    g3: Circle CenterX=96.5 CenterY=16.75 CenterZ=0 NormalX=0 NormalY=0 NormalZ=1 AngleXU=0 Radius=3.25
  constraints (10):
    c: Coincident(g0,g-3)
    c: Coincident(g1,g-4)
    c: Equal(g0,g1)
    c: Equal(g1,g2)
    c: Equal(g2,g3)
    c: Diameter(g0) = 6.5
    c: Horizontal(g3,g1)
    c: Horizontal(g2,g0)
    c: Vertical(g2,g3)
    c: DistanceX(g1,g3) = 93
FEATURE [PartDesign::Pocket] Pocket099
  BaseFeature = -> Pad118
  Direction = (0,0,-1)
  Length = 2
  Length2 = 5
  Profile = -> Sketch243
  ReferenceAxis = -> Sketch243 [N_Axis]
  Refine = true
  Suppressed = false
  Type = 0
FEATURE [PartDesign::Body] Body083  label="pince_capot001"
  AllowCompound = false
  Group = -> [Sketch242,Pad118,Sketch243,Pocket099]
  Origin = -> Origin284
  Placement = pos=(-25,-5,28) rot=(0,0,1;0rad)
  Tip = -> Pocket099
COMPONENT P3 — recipe-attached ("pince_cremaillere_bras002", modeled in this document).
Construction recipe (the document's own serialized feature program — sketch geometry with constraints, then the solid features built on it; lengths are millimeters unless a unit is written):

FEATURE [PartDesign::FeatureBase] BaseFeature002
  BaseFeature = -> InvoluteRack001
  Suppressed = false
FEATURE [Sketcher::SketchObject] Sketch244
  ArcFitTolerance = 1e-06
  AttachmentSupport = -> [BaseFeature002]
  FullyConstrained = true
  MakeInternals = false
  MapMode = 5
  Placement = pos=(0,92.677,0) rot=(0,0.707107,0.707107;3.14159rad)
  sketch-geometry (4):
    g0: LineSegment StartX=-29.25 StartY=0 StartZ=0 EndX=10.75 EndY=0 EndZ=0
    g1: LineSegment StartX=10.75 StartY=0 StartZ=0 EndX=10.75 EndY=40 EndZ=0
    g2: LineSegment StartX=10.75 StartY=40 StartZ=0 EndX=-29.25 EndY=40 EndZ=0
    g3: LineSegment StartX=-29.25 StartY=40 StartZ=0 EndX=-29.25 EndY=0 EndZ=0
  constraints (12):
    c: Coincident(g0,g1)
    c: Coincident(g1,g2)
    c: Coincident(g2,g3)
    c: Coincident(g3,g0)
    c: Horizontal(g0)
    c: Horizontal(g2)
    c: Vertical(g1)
    c: Vertical(g3)
    c: DistanceY(g3,g3) = 40
    c: DistanceX(g2,g2) = 40
    c: PointOnObject(g0,g-1)
    c: DistanceX(g-1,g0) = 10.75
FEATURE [PartDesign::Pad] Pad119
  BaseFeature = -> BaseFeature002
  Direction = (0,1,-2e-16)
  Length = 5
  Length2 = 10
  Profile = -> Sketch244
  ReferenceAxis = -> Sketch244 [N_Axis]
  Refine = true
  Suppressed = false
  Type = 0
FEATURE [Sketcher::SketchObject] Sketch262
  ArcFitTolerance = 1e-06
  AttachmentOffset = pos=(0,0,-10.75) rot=(0,0,1;0rad)
  AttachmentSupport = -> [YZ_Plane282]
  ExternalGeometry = -> [Pad119]
  FullyConstrained = true
  MakeInternals = false
  MapMode = 5
  Placement = pos=(-10.75,0,0) rot=(0.57735,0.57735,0.57735;2.0944rad)
  sketch-geometry (3):
    g0: LineSegment StartX=67.677 StartY=3 StartZ=0 EndX=92.677 EndY=9 EndZ=0
    g1: LineSegment StartX=67.677 StartY=3 StartZ=0 EndX=92.677 EndY=3 EndZ=0
    g2: LineSegment StartX=92.677 StartY=9 StartZ=0 EndX=92.677 EndY=3 EndZ=0
  constraints (8):
    c: PointOnObject(g0,g-4)
    c: Coincident(g1,g0)
    c: Coincident(g1,g-4)
    c: Coincident(g2,g0)
    c: Coincident(g2,g1)
    c: DistanceX(g1,g1) = 25
    c: Vertical(g2)
    c: DistanceY(g2,g2) = 6
FEATURE [PartDesign::Pad] Pad124
  BaseFeature = -> Pad119
  Direction = (1,0,0)
  Length = 5
  Length2 = 10
  Profile = -> Sketch262
  ReferenceAxis = -> Sketch262 [N_Axis]
  Suppressed = false
  Type = 0
FEATURE [PartDesign::Body] Body084  label="pince_cremaillere_bras002"
  AllowCompound = false
  BaseFeature = -> InvoluteRack001
  Group = -> [BaseFeature002,Sketch244,Pad119,Sketch262,Pad124]
  Origin = -> Origin285
  Placement = pos=(-18.1714,32.25,24) rot=(0,0,-1;1.5708rad)
  Tip = -> Pad124
COMPONENT P4 — recipe-attached ("pince_support_servo001", modeled in this document).
Construction recipe (the document's own serialized feature program — sketch geometry with constraints, then the solid features built on it; lengths are millimeters unless a unit is written):

FEATURE [Sketcher::SketchObject] Sketch245
  ArcFitTolerance = 0
  AttachmentOffset = pos=(0,0,-2) rot=(0,0,1;0rad)
  AttachmentSupport = -> [XY_Plane283]
  FullyConstrained = true
  MakeInternals = false
  MapMode = 2
  Placement = pos=(0,0,-2) rot=(0,0,1;0rad)
  sketch-geometry (18):
    g0: LineSegment StartX=14.5 StartY=50 StartZ=0 EndX=35.5 EndY=50 EndZ=0
    g1: LineSegment StartX=35.5 StartY=50 StartZ=0 EndX=35.5 EndY=9 EndZ=0
    g2: LineSegment StartX=35.5 StartY=9 StartZ=0 EndX=14.5 EndY=9 EndZ=0
    g3: LineSegment StartX=14.5 StartY=9 StartZ=0 EndX=14.5 EndY=50 EndZ=0
    g4: LineSegment StartX=0 StartY=59 StartZ=0 EndX=50 EndY=59 EndZ=0
    g5: LineSegment StartX=50 StartY=59 StartZ=0 EndX=50 EndY=0 EndZ=0
    g6: LineSegment StartX=50 StartY=0 StartZ=0 EndX=0 EndY=0 EndZ=0
    g7: LineSegment StartX=0 StartY=0 StartZ=0 EndX=0 EndY=59 EndZ=0
    g8: Circle CenterX=19 CenterY=54.5 CenterZ=0 NormalX=0 NormalY=0 NormalZ=1 AngleXU=0 Radius=1.65
    g9: Circle CenterX=31 CenterY=54.5 CenterZ=0 NormalX=0 NormalY=0 NormalZ=1 AngleXU=0 Radius=1.65
    g10: Circle CenterX=19 CenterY=4.5 CenterZ=0 NormalX=0 NormalY=0 NormalZ=1 AngleXU=0 Radius=1.65
    g11: Circle CenterX=31 CenterY=4.5 CenterZ=0 NormalX=0 NormalY=0 NormalZ=1 AngleXU=0 Radius=1.65
    g12: LineSegment [constr] StartX=19 StartY=54.5 StartZ=0 EndX=31 EndY=54.5 EndZ=0
    g13: LineSegment [constr] StartX=31 StartY=54.5 StartZ=0 EndX=31 EndY=4.5 EndZ=0
    g14: LineSegment [constr] StartX=31 StartY=4.5 StartZ=0 EndX=19 EndY=4.5 EndZ=0
    g15: LineSegment [constr] StartX=19 StartY=4.5 StartZ=0 EndX=19 EndY=54.5 EndZ=0
    g16: LineSegment [constr] StartX=14.5 StartY=29.5 StartZ=0 EndX=35.5 EndY=29.5 EndZ=0
    g17: LineSegment [constr] StartX=25 StartY=50 StartZ=0 EndX=25 EndY=9 EndZ=0
  constraints (46):
    c: Coincident(g0,g1)
    c: Coincident(g1,g2)
    c: Coincident(g2,g3)
    c: Coincident(g3,g0)
    c: Horizontal(g0)
    c: Horizontal(g2)
    c: Vertical(g1)
    c: Vertical(g3)
    c: Coincident(g4,g5)
    c: Coincident(g5,g6)
    c: Coincident(g6,g7)
    c: Coincident(g7,g4)
    c: Horizontal(g6)
    c: Vertical(g5)
    c: Coincident(g12,g13)
    c: Coincident(g13,g14)
    c: Coincident(g14,g15)
    c: Coincident(g15,g12)
    c: Horizontal(g14)
    c: Vertical(g15)
    c: Coincident(g10,g14)
    c: Coincident(g11,g13)
    c: Coincident(g8,g12)
    c: Coincident(g9,g12)
    c: PointOnObject(g17,g0)
    c: PointOnObject(g17,g2)
    c: PointOnObject(g16,g3)
    c: PointOnObject(g16,g1)
    c: Symmetric(g0,g0,g17)
    c: Symmetric(g2,g0,g16)
    c: Symmetric(g9,g8,g17)
    c: DistanceX(g2,g2) = 21
    c: DistanceY(g3,g3) = 41
    c: DistanceX(g14,g14) = 12
    c: DistanceY(g13,g13) = 50
    c: Equal(g9,g8)
    c: Equal(g9,g11)
    c: Equal(g9,g10)
    c: Diameter(g9) = 3.3
    c: Symmetric(g9,g11,g16)
    c: Coincident(g-1,g6)
    c: Symmetric(g4,g4,g17)
    c: DistanceX(g6,g2) = 14.5
    c: Vertical(g7)
    c: DistanceY(g5,g5) = 59
    c: DistanceY(g-1,g2) = 9
FEATURE [PartDesign::Pad] Pad120
  AlongSketchNormal = false
  Direction = (0,0,1)
  Length = 4
  Length2 = 100
  Profile = -> Sketch245
  ReferenceAxis = -> Sketch245 [N_Axis]
  Suppressed = false
  Type = 0
FEATURE [Sketcher::SketchObject] Sketch246
  ArcFitTolerance = 0
  AttachmentSupport = -> [Pad120]
  ExternalGeometry = -> [Pad120]
  FullyConstrained = true
  MakeInternals = false
  MapMode = 5
  Placement = pos=(0,0,2) rot=(0,0,1;0rad)
  sketch-geometry (10):
    g0: LineSegment StartX=0 StartY=40 StartZ=0 EndX=8 EndY=40 EndZ=0
    g1: LineSegment StartX=8 StartY=40 StartZ=0 EndX=8 EndY=0 EndZ=0
    g2: LineSegment StartX=8 StartY=0 StartZ=0 EndX=0 EndY=0 EndZ=0
    g3: LineSegment StartX=0 StartY=0 StartZ=0 EndX=0 EndY=40 EndZ=0
    g4: LineSegment StartX=42 StartY=40 StartZ=0 EndX=50 EndY=40 EndZ=0
    g5: LineSegment StartX=50 StartY=40 StartZ=0 EndX=50 EndY=0 EndZ=0
    g6: LineSegment StartX=50 StartY=0 StartZ=0 EndX=42 EndY=0 EndZ=0
    g7: LineSegment StartX=42 StartY=0 StartZ=0 EndX=42 EndY=40 EndZ=0
    g8: LineSegment [constr] StartX=25 StartY=59 StartZ=0 EndX=25 EndY=0 EndZ=0
    g9: LineSegment [constr] StartX=0 StartY=20 StartZ=0 EndX=50 EndY=20 EndZ=0
  constraints (28):
    c: Coincident(g0,g1)
    c: Coincident(g1,g2)
    c: Coincident(g2,g3)
    c: Coincident(g3,g0)
    c: Horizontal(g0)
    c: Horizontal(g2)
    c: Vertical(g3)
    c: Coincident(g4,g5)
    c: Coincident(g5,g6)
    c: Coincident(g6,g7)
    c: Coincident(g7,g4)
    c: Horizontal(g4)
    c: Horizontal(g6)
    c: Vertical(g5)
    c: PointOnObject(g4,g-4)
    c: PointOnObject(g8,g-5)
    c: PointOnObject(g8,g-6)
    c: Symmetric(g-5,g-5,g8)
    c: Symmetric(g0,g4,g8)
    c: DistanceX(g0,g0) = 8
    c: Vertical(g1)
    c: PointOnObject(g9,g3)
    c: PointOnObject(g9,g5)
    c: Symmetric(g0,g1,g9)
    c: Vertical(g7)
    c: PointOnObject(g5,g-1)
    c: DistanceY(g3,g3) = 40
    c: Coincident(g2,g-1)
FEATURE [PartDesign::Pad] Pad121
  AlongSketchNormal = false
  BaseFeature = -> Pad120
  Direction = (0,0,1)
  Length = 18
  Length2 = 100
  Profile = -> Sketch246
  Suppressed = false
  Type = 0
FEATURE [Sketcher::SketchObject] Sketch247
  ArcFitTolerance = 0
  AttachmentSupport = -> [Pad121]
  ExternalGeometry = -> [Pad121]
  FullyConstrained = true
  MakeInternals = false
  MapMode = 5
  Placement = pos=(0,0,20) rot=(0,0,1;0rad)
  sketch-geometry (7):
    g0: LineSegment [constr] StartX=25 StartY=40 StartZ=0 EndX=25 EndY=0 EndZ=0
    g1: LineSegment [constr] StartX=0 StartY=20 StartZ=0 EndX=50 EndY=20 EndZ=0
    g2: Circle CenterX=4 CenterY=36 CenterZ=0 NormalX=0 NormalY=0 NormalZ=1 AngleXU=0 Radius=1.75
    g3: Circle CenterX=46 CenterY=36 CenterZ=0 NormalX=0 NormalY=0 NormalZ=1 AngleXU=0 Radius=1.75
    g4: Circle CenterX=4 CenterY=4 CenterZ=0 NormalX=0 NormalY=0 NormalZ=1 AngleXU=0 Radius=1.75
    g5: Circle CenterX=46 CenterY=4 CenterZ=0 NormalX=0 NormalY=0 NormalZ=1 AngleXU=0 Radius=1.75
    g6: LineSegment [constr] StartX=4 StartY=36 StartZ=0 EndX=4 EndY=4 EndZ=0
  constraints (17):
    c: PointOnObject(g0,g-4)
    c: PointOnObject(g0,g-5)
    c: PointOnObject(g1,g-7)
    c: PointOnObject(g1,g-8)
    c: Symmetric(g-3,g-4,g0)
    c: Symmetric(g-5,g-4,g1)
    c: Symmetric(g4,g2,g1)
    c: Symmetric(g3,g2,g0)
    c: Symmetric(g5,g3,g1)
    c: Equal(g2,g4)
    c: Equal(g2,g3)
    c: Equal(g2,g5)
    c: Radius(g2) = 1.75
    c: Coincident(g6,g4)
    c: Coincident(g6,g2)
    c: Symmetric(g-7,g-5,g6)
    c: DistanceY(g-5,g4) = 4
FEATURE [PartDesign::Pocket] Pocket100
  BaseFeature = -> Pad121
  Direction = (0,0,-1)
  Length = 5
  Length2 = 100
  Profile = -> Sketch247
  Suppressed = false
  Type = 1
FEATURE [Sketcher::SketchObject] Sketch248
  ArcFitTolerance = 0
  AttachmentSupport = -> [Pocket100]
  ExternalGeometry = -> [Pocket100]
  FullyConstrained = true
  MakeInternals = false
  MapMode = 5
  Placement = pos=(50,0,0) rot=(0.57735,0.57735,0.57735;2.0944rad)
  sketch-geometry (7):
    g0: LineSegment [constr] StartX=0 StartY=20 StartZ=0 EndX=40 EndY=0 EndZ=0
    g1: LineSegment [constr] StartX=0 StartY=0 StartZ=0 EndX=40 EndY=20 EndZ=0
    g2: Circle CenterX=12 CenterY=17 CenterZ=0 NormalX=0 NormalY=0 NormalZ=1 AngleXU=0 Radius=1.75
    g3: Circle CenterX=12 CenterY=3 CenterZ=0 NormalX=0 NormalY=0 NormalZ=1 AngleXU=0 Radius=1.75
    g4: Circle CenterX=28 CenterY=3 CenterZ=0 NormalX=0 NormalY=0 NormalZ=1 AngleXU=0 Radius=1.75
    g5: Circle CenterX=28 CenterY=17 CenterZ=0 NormalX=0 NormalY=0 NormalZ=1 AngleXU=0 Radius=1.75
    g6: GeomPoint X=20 Y=10 Z=0
  constraints (19):
    c: Equal(g3,g2)
    c: Equal(g3,g5)
    c: Equal(g3,g4)
    c: Coincident(g0,g-5)
    c: Coincident(g1,g-4)
    c: DistanceX(g-3,g-3) = 40
    c: Horizontal(g2,g5)
    c: Horizontal(g3,g4)
    c: Diameter(g3) = 3.5
    c: Vertical(g3,g2)
    c: Vertical(g5,g4)
    c: PointOnObject(g6,g0)
    c: PointOnObject(g6,g1)
    c: DistanceX(g2,g6) = 8
    c: DistanceY(g6,g2) = 7
    c: Symmetric(g2,g4,g6)
    c: Coincident(g1,g-1)
    c: PointOnObject(g0,g-1)
    c: Vertical(g-4,g0)
FEATURE [PartDesign::Pocket] Pocket101
  BaseFeature = -> Pocket100
  Direction = (-1,0,0)
  Length = 5
  Length2 = 100
  Profile = -> Sketch248
  ReferenceAxis = -> Sketch248 [N_Axis]
  Suppressed = false
  Type = 1
FEATURE [Sketcher::SketchObject] Sketch249
  ArcFitTolerance = 1e-06
  AttachmentSupport = -> [Pocket101]
  ExternalGeometry = -> [Pocket101]
  FullyConstrained = true
  MakeInternals = false
  MapMode = 5
  Placement = pos=(50,0,0) rot=(0.57735,0.57735,0.57735;2.0944rad)
  sketch-geometry (4):
    g0: Circle CenterX=12 CenterY=17 CenterZ=0 NormalX=0 NormalY=0 NormalZ=1 AngleXU=0 Radius=2.125
    g1: Circle CenterX=28 CenterY=17 CenterZ=0 NormalX=0 NormalY=0 NormalZ=1 AngleXU=0 Radius=2.125
    g2: Circle CenterX=28 CenterY=3 CenterZ=0 NormalX=0 NormalY=0 NormalZ=1 AngleXU=0 Radius=2.125
    g3: Circle CenterX=12 CenterY=3 CenterZ=0 NormalX=0 NormalY=0 NormalZ=1 AngleXU=0 Radius=2.125
  constraints (8):
    c: Equal(g0,g1)
    c: Equal(g1,g3)
    c: Equal(g3,g2)
    c: Diameter(g0) = 4.25
    c: Coincident(g0,g-3)
    c: Coincident(g-4,g1)
    c: Coincident(g-5,g2)
    c: Coincident(g-6,g3)
FEATURE [PartDesign::Pocket] Pocket102
  BaseFeature = -> Pocket101
  Direction = (-1,0,0)
  Length = 1.5
  Length2 = 5
  Profile = -> Sketch249
  ReferenceAxis = -> Sketch249 [N_Axis]
  Refine = true
  Suppressed = false
  Type = 0
FEATURE [Sketcher::SketchObject] Sketch250
  ArcFitTolerance = 1e-06
  AttachmentSupport = -> [Pocket102]
  ExternalGeometry = -> [Pocket102]
  FullyConstrained = true
  MakeInternals = false
  MapMode = 5
  Placement = pos=(0,0,0) rot=(0.57735,-0.57735,-0.57735;2.0944rad)
  sketch-geometry (4):
    g0: Circle CenterX=-28 CenterY=17 CenterZ=0 NormalX=0 NormalY=0 NormalZ=1 AngleXU=0 Radius=2.1
    g1: Circle CenterX=-12 CenterY=17 CenterZ=0 NormalX=0 NormalY=0 NormalZ=1 AngleXU=0 Radius=2.1
    g2: Circle CenterX=-12 CenterY=3 CenterZ=0 NormalX=0 NormalY=0 NormalZ=1 AngleXU=0 Radius=2.1
    g3: Circle CenterX=-28 CenterY=3 CenterZ=0 NormalX=0 NormalY=0 NormalZ=1 AngleXU=0 Radius=2.1
  constraints (8):
    c: Equal(g0,g1)
    c: Equal(g1,g3)
    c: Equal(g3,g2)
    c: Diameter(g0) = 4.2
    c: Coincident(g0,g-3)
    c: Coincident(g-4,g1)
    c: Coincident(g-5,g2)
    c: Coincident(g3,g-6)
FEATURE [PartDesign::Pocket] Pocket103
  BaseFeature = -> Pocket102
  Direction = (1,0,0)
  Length = 1.5
  Length2 = 5
  Profile = -> Sketch250
  ReferenceAxis = -> Sketch250 [N_Axis]
  Refine = true
  Suppressed = false
  Type = 0
FEATURE [Sketcher::SketchObject] Sketch251
  ArcFitTolerance = 1e-06
  AttachmentSupport = -> [Pocket103]
  ExternalGeometry = -> [Pocket103]
  FullyConstrained = true
  MakeInternals = false
  MapMode = 5
  Placement = pos=(0,0,20) rot=(0,0,1;0rad)
  sketch-geometry (4):
    g0: Circle CenterX=4 CenterY=36 CenterZ=0 NormalX=0 NormalY=0 NormalZ=1 AngleXU=0 Radius=2.1
    g1: Circle CenterX=46 CenterY=36 CenterZ=0 NormalX=0 NormalY=0 NormalZ=1 AngleXU=0 Radius=2.1
    g2: Circle CenterX=4 CenterY=4 CenterZ=0 NormalX=0 NormalY=0 NormalZ=1 AngleXU=0 Radius=2.1
    g3: Circle CenterX=46 CenterY=4 CenterZ=0 NormalX=0 NormalY=0 NormalZ=1 AngleXU=0 Radius=2.1
  constraints (8):
    c: Coincident(g0,g-3)
    c: Coincident(g1,g-6)
    c: Coincident(g2,g-4)
    c: Coincident(g3,g-5)
    c: Equal(g0,g2)
    c: Equal(g2,g1)
    c: Equal(g1,g3)
    c: Diameter(g0) = 4.2
FEATURE [PartDesign::Pocket] Pocket104
  BaseFeature = -> Pocket103
  Direction = (0,0,-1)
  Length = 1.5
  Length2 = 5
  Profile = -> Sketch251
  ReferenceAxis = -> Sketch251 [N_Axis]
  Refine = true
  Suppressed = false
  Type = 0
FEATURE [Sketcher::SketchObject] Sketch252
  ArcFitTolerance = 1e-06
  AttachmentSupport = -> [Pocket104]
  ExternalGeometry = -> [Pocket104]
  FullyConstrained = true
  MakeInternals = false
  MapMode = 5
  Placement = pos=(0,0,-2) rot=(1,0,0;3.14159rad)
  sketch-geometry (4):
    g0: Circle CenterX=4 CenterY=-4 CenterZ=0 NormalX=0 NormalY=0 NormalZ=1 AngleXU=0 Radius=2.1
    g1: Circle CenterX=46 CenterY=-4 CenterZ=0 NormalX=0 NormalY=0 NormalZ=1 AngleXU=0 Radius=2.1
    g2: Circle CenterX=46 CenterY=-36 CenterZ=0 NormalX=0 NormalY=0 NormalZ=1 AngleXU=0 Radius=2.1
    g3: Circle CenterX=4 CenterY=-36 CenterZ=0 NormalX=0 NormalY=0 NormalZ=1 AngleXU=0 Radius=2.1
  constraints (8):
    c: Coincident(g0,g-3)
    c: Coincident(g1,g-5)
    c: Coincident(g2,g-6)
    c: Coincident(g3,g-4)
    c: Equal(g0,g1)
    c: Equal(g1,g2)
    c: Equal(g2,g3)
    c: Diameter(g0) = 4.2
FEATURE [PartDesign::Pocket] Pocket105
  BaseFeature = -> Pocket104
  Direction = (0,0,1)
  Length = 1.5
  Length2 = 5
  Profile = -> Sketch252
  ReferenceAxis = -> Sketch252 [N_Axis]
  Refine = true
  Suppressed = false
  Type = 0
FEATURE [PartDesign::Body] Body085  label="pince_support_servo001"
  AllowCompound = false
  Group = -> [Sketch245,Pad120,Sketch246,Pad121,Sketch247,Pocket100,Sketch248,Pocket101,Sketch249,Pocket102,Sketch250,Pocket103,Sketch251,Pocket104,Sketch252,Pocket105]
  Origin = -> Origin286
  Tip = -> Pocket105
COMPONENT P5 — recipe-attached ("pince_cremaillere_pignon001", modeled in this document).
Construction recipe (the document's own serialized feature program — sketch geometry with constraints, then the solid features built on it; lengths are millimeters unless a unit is written):

FEATURE [PartDesign::FeatureBase] BaseFeature003
  BaseFeature = -> InvoluteGear001
  Suppressed = false
FEATURE [Sketcher::SketchObject] Sketch253
  ArcFitTolerance = 0
  FullyConstrained = true
  MakeInternals = false
  MapMode = 5
  Placement = pos=(0,0,5.5) rot=(0,0,1;0rad)
  sketch-geometry (8):
    g0: Circle [constr] CenterX=0 CenterY=0 CenterZ=0 NormalX=0 NormalY=0 NormalZ=1 AngleXU=0 Radius=7
    g1: Circle CenterX=0 CenterY=7 CenterZ=0 NormalX=0 NormalY=0 NormalZ=1 AngleXU=0 Radius=1.65
    g2: Circle CenterX=-7 CenterY=0 CenterZ=0 NormalX=0 NormalY=0 NormalZ=1 AngleXU=0 Radius=1.65
    g3: Circle CenterX=7 CenterY=0 CenterZ=0 NormalX=0 NormalY=0 NormalZ=1 AngleXU=0 Radius=1.65
    g4: Circle CenterX=0 CenterY=-7 CenterZ=0 NormalX=0 NormalY=0 NormalZ=1 AngleXU=0 Radius=1.65
    g5: Circle CenterX=0 CenterY=0 CenterZ=0 NormalX=0 NormalY=0 NormalZ=1 AngleXU=0 Radius=3
    g6: LineSegment [constr] StartX=-7 StartY=0 StartZ=0 EndX=7 EndY=0 EndZ=0
    g7: LineSegment [constr] StartX=0 StartY=7 StartZ=0 EndX=0 EndY=-7 EndZ=0
  constraints (20):
    c: Coincident(g5,g0)
    c: Coincident(g5,g-1)
    c: PointOnObject(g2,g0)
    c: PointOnObject(g1,g0)
    c: PointOnObject(g3,g0)
    c: PointOnObject(g4,g0)
    c: Coincident(g2,g6)
    c: Coincident(g1,g7)
    c: Coincident(g6,g3)
    c: Coincident(g7,g4)
    c: PointOnObject(g5,g7)
    c: PointOnObject(g5,g6)
    c: Perpendicular(g7,g6)
    c: Equal(g1,g3)
    c: Equal(g1,g2)
    c: Equal(g1,g4)
    c: Diameter(g1) = 3.3
    c: Diameter(g5) = 6
    c: Diameter(g0) = 14
    c: PointOnObject(g2,g-1)
FEATURE [PartDesign::Pocket] Pocket106
  BaseFeature = -> BaseFeature003
  Direction = (0,0,-1)
  Length = 5
  Length2 = 100
  Profile = -> Sketch253
  Suppressed = false
  Type = 1
FEATURE [Sketcher::SketchObject] Sketch254
  ArcFitTolerance = 0
  AttachmentSupport = -> [Pocket106]
  ExternalGeometry = -> [Pocket106]
  FullyConstrained = true
  MakeInternals = false
  MapMode = 5
  Placement = pos=(0,0,0) rot=(1,0,0;3.14159rad)
  sketch-geometry (4):
    g0: Circle CenterX=0 CenterY=-7 CenterZ=0 NormalX=0 NormalY=0 NormalZ=1 AngleXU=0 Radius=3.25
    g1: Circle CenterX=-7 CenterY=0 CenterZ=0 NormalX=0 NormalY=0 NormalZ=1 AngleXU=0 Radius=3.25
    g2: Circle CenterX=7 CenterY=0 CenterZ=0 NormalX=0 NormalY=0 NormalZ=1 AngleXU=0 Radius=3.25
    g3: Circle CenterX=0 CenterY=7 CenterZ=0 NormalX=0 NormalY=0 NormalZ=1 AngleXU=0 Radius=3.25
  constraints (8):
    c: Coincident(g1,g-5)
    c: Coincident(g0,g-3)
    c: Coincident(g2,g-4)
    c: Coincident(g3,g-6)
    c: Equal(g2,g0)
    c: Equal(g2,g1)
    c: Equal(g2,g3)
    c: Diameter(g2) = 6.5
FEATURE [PartDesign::Pocket] Pocket107
  BaseFeature = -> Pocket106
  Direction = (0,0,1)
  Length = 3.5
  Length2 = 100
  Profile = -> Sketch254
  Suppressed = false
  Type = 0
FEATURE [PartDesign::Body] Body086  label="pince_cremaillere_pignon001"
  AllowCompound = false
  BaseFeature = -> InvoluteGear001
  Group = -> [BaseFeature003,Sketch253,Pocket106,Sketch254,Pocket107]
  Origin = -> Origin287
  Placement = pos=(25,20,27.098) rot=(0.715163,-0.698958,0;3.14159rad)
  Tip = -> Pocket107
COMPONENT P6 — recipe-attached ("pince_support_cremaillere001", modeled in this document).
Construction recipe (the document's own serialized feature program — sketch geometry with constraints, then the solid features built on it; lengths are millimeters unless a unit is written):

FEATURE [Sketcher::SketchObject] Sketch255
  ArcFitTolerance = 0
  FullyConstrained = true
  MakeInternals = false
  MapMode = 2
  sketch-geometry (25):
    g0: LineSegment StartX=0 StartY=50 StartZ=0 EndX=100 EndY=50 EndZ=0
    g1: LineSegment StartX=100 StartY=50 StartZ=0 EndX=100 EndY=0 EndZ=0
    g2: LineSegment StartX=100 StartY=0 StartZ=0 EndX=0 EndY=0 EndZ=0
    g3: LineSegment StartX=0 StartY=0 StartZ=0 EndX=0 EndY=50 EndZ=0
    g4: Circle CenterX=50 CenterY=25 CenterZ=0 NormalX=0 NormalY=0 NormalZ=1 AngleXU=0 Radius=14
    g5: LineSegment [constr] StartX=0 StartY=50 StartZ=0 EndX=100 EndY=0 EndZ=0
    g6: LineSegment [constr] StartX=0 StartY=0 StartZ=0 EndX=100 EndY=50 EndZ=0
    g7: LineSegment [constr] StartX=29 StartY=41 StartZ=0 EndX=71 EndY=41 EndZ=0
    g8: LineSegment [constr] StartX=71 StartY=41 StartZ=0 EndX=71 EndY=9 EndZ=0
    g9: LineSegment [constr] StartX=71 StartY=9 StartZ=0 EndX=29 EndY=9 EndZ=0
    g10: LineSegment [constr] StartX=29 StartY=9 StartZ=0 EndX=29 EndY=41 EndZ=0
    g11: Circle CenterX=29 CenterY=41 CenterZ=0 NormalX=0 NormalY=0 NormalZ=1 AngleXU=0 Radius=1.75
    g12: Circle CenterX=71 CenterY=41 CenterZ=0 NormalX=0 NormalY=0 NormalZ=1 AngleXU=0 Radius=1.75
    g13: Circle CenterX=71 CenterY=9 CenterZ=0 NormalX=0 NormalY=0 NormalZ=1 AngleXU=0 Radius=1.75
    g14: Circle CenterX=29 CenterY=9 CenterZ=0 NormalX=0 NormalY=0 NormalZ=1 AngleXU=0 Radius=1.75
    g15: LineSegment [constr] StartX=0 StartY=25 StartZ=0 EndX=100 EndY=25 EndZ=0
    g16: LineSegment [constr] StartX=50 StartY=50 StartZ=0 EndX=50 EndY=0 EndZ=0
    g17: LineSegment [constr] StartX=3.5 StartY=33.25 StartZ=0 EndX=96.5 EndY=33.25 EndZ=0
    g18: LineSegment [constr] StartX=96.5 StartY=33.25 StartZ=0 EndX=96.5 EndY=16.75 EndZ=0
    g19: LineSegment [constr] StartX=96.5 StartY=16.75 StartZ=0 EndX=3.5 EndY=16.75 EndZ=0
    g20: LineSegment [constr] StartX=3.5 StartY=16.75 StartZ=0 EndX=3.5 EndY=33.25 EndZ=0
    g21: Circle CenterX=96.5 CenterY=33.25 CenterZ=0 NormalX=0 NormalY=0 NormalZ=1 AngleXU=0 Radius=1.65
    g22: Circle CenterX=3.5 CenterY=33.25 CenterZ=0 NormalX=0 NormalY=0 NormalZ=1 AngleXU=0 Radius=1.65
    g23: Circle CenterX=3.5 CenterY=16.75 CenterZ=0 NormalX=0 NormalY=0 NormalZ=1 AngleXU=0 Radius=1.65
    g24: Circle CenterX=96.5 CenterY=16.75 CenterZ=0 NormalX=0 NormalY=0 NormalZ=1 AngleXU=0 Radius=1.65
  constraints (60):
    c: Coincident(g0,g1)
    c: Coincident(g1,g2)
    c: Coincident(g2,g3)
    c: Coincident(g3,g0)
    c: Horizontal(g0)
    c: Horizontal(g2)
    c: Vertical(g1)
    c: Vertical(g3)
    c: Coincident(g2,g-1)
    c: Coincident(g5,g0)
    c: Coincident(g2,g6)
    c: Coincident(g0,g6)
    c: Coincident(g1,g5)
    c: PointOnObject(g4,g6)
    c: PointOnObject(g4,g5)
    c: Diameter(g4) = 28
    c: DistanceY(g3,g3) = 50
    c: DistanceX(g2,g2) = 100
    c: Coincident(g7,g8)
    c: Coincident(g8,g9)
    c: Coincident(g9,g10)
    c: Coincident(g10,g7)
    c: Horizontal(g7)
    c: Vertical(g10)
    c: Coincident(g11,g7)
    c: Coincident(g7,g12)
    c: Coincident(g9,g14)
    c: Coincident(g8,g13)
    c: Equal(g11,g12)
    c: Equal(g11,g14)
    c: Equal(g11,g13)
    c: Radius(g11) = 1.75
    c: DistanceY(g10,g10) = 32
    c: DistanceX(g7,g7) = 42
    c: PointOnObject(g16,g0)
    c: PointOnObject(g15,g1)
    c: PointOnObject(g15,g3)
    c: PointOnObject(g16,g2)
    c: Symmetric(g0,g0,g16)
    c: Symmetric(g0,g2,g15)
    c: Symmetric(g14,g13,g16)
    c: Symmetric(g12,g13,g15)
    c: Coincident(g17,g18)
    c: Coincident(g18,g19)
    c: Coincident(g19,g20)
    c: Coincident(g20,g17)
    c: Horizontal(g19)
    c: Vertical(g20)
    c: Symmetric(g17,g18,g15)
    c: Symmetric(g17,g17,g16)
    c: Distance(g20) = 16.5
    c: DistanceX(g0,g17) = 3.5
    c: Coincident(g24,g18)
    c: Coincident(g21,g17)
    c: Coincident(g17,g22)
    c: Coincident(g19,g23)
    c: Equal(g22,g23)
    c: Equal(g22,g21)
    c: Equal(g22,g24)
    c: Diameter(g22) = 3.3
FEATURE [PartDesign::Pad] Pad122
  AlongSketchNormal = false
  Direction = (0,0,1)
  Length = 8
  Length2 = 100
  Profile = -> Sketch255
  Suppressed = false
  Type = 0
FEATURE [Sketcher::SketchObject] Sketch256
  ArcFitTolerance = 0
  AttachmentSupport = -> [Pad122]
  ExternalGeometry = -> [Pad122]
  FullyConstrained = true
  MakeInternals = false
  MapMode = 5
  Placement = pos=(0,0,8) rot=(0,0,1;0rad)
  sketch-geometry (9):
    g0: LineSegment StartX=0 StartY=48 StartZ=0 EndX=100 EndY=48 EndZ=0
    g1: LineSegment StartX=100 StartY=48 StartZ=0 EndX=100 EndY=35.75 EndZ=0
    g2: LineSegment StartX=100 StartY=35.75 StartZ=0 EndX=0 EndY=35.75 EndZ=0
    g3: LineSegment StartX=0 StartY=35.75 StartZ=0 EndX=0 EndY=48 EndZ=0
    g4: LineSegment StartX=0 StartY=2 StartZ=0 EndX=100 EndY=2 EndZ=0
    g5: LineSegment StartX=100 StartY=2 StartZ=0 EndX=100 EndY=14.25 EndZ=0
    g6: LineSegment StartX=100 StartY=14.25 StartZ=0 EndX=0 EndY=14.25 EndZ=0
    g7: LineSegment StartX=0 StartY=14.25 StartZ=0 EndX=0 EndY=2 EndZ=0
    g8: Circle [constr] CenterX=50 CenterY=25 CenterZ=0 NormalX=0 NormalY=0 NormalZ=1 AngleXU=0 Radius=10.75
  constraints (26):
    c: Coincident(g0,g1)
    c: Coincident(g1,g2)
    c: Coincident(g2,g3)
    c: Coincident(g3,g0)
    c: Horizontal(g0)
    c: Horizontal(g2)
    c: Vertical(g1)
    c: Vertical(g3)
    c: Coincident(g4,g5)
    c: Coincident(g5,g6)
    c: Coincident(g6,g7)
    c: Coincident(g7,g4)
    c: Horizontal(g4)
    c: Horizontal(g6)
    c: Vertical(g5)
    c: Vertical(g7)
    c: PointOnObject(g6,g-6)
    c: PointOnObject(g2,g-6)
    c: PointOnObject(g1,g-5)
    c: PointOnObject(g5,g-5)
    c: Coincident(g8,g-7)
    c: Diameter(g8) = 21.5
    c: Tangent(g8,g2)
    c: Tangent(g6,g8)
    c: Equal(g7,g3)
    c: DistanceY(g0,g-6) = 2
FEATURE [PartDesign::Pocket] Pocket108
  BaseFeature = -> Pad122
  Direction = (0,0,-1)
  Length = 4
  Length2 = 100
  Profile = -> Sketch256
  Suppressed = false
  Type = 0
FEATURE [Sketcher::SketchObject] Sketch257
  ArcFitTolerance = 0
  AttachmentSupport = -> [Pocket108]
  ExternalGeometry = -> [Pocket108]
  FullyConstrained = true
  MakeInternals = false
  MapMode = 5
  Placement = pos=(0,0,8) rot=(0,0,1;0rad)
  sketch-geometry (10):
    g0: ArcOfCircle CenterX=11 CenterY=25 CenterZ=0 NormalX=0 NormalY=0 NormalZ=1 AngleXU=0 Radius=8 StartAngle=1.5708 EndAngle=4.71239
    g1: ArcOfCircle CenterX=26 CenterY=25 CenterZ=0 NormalX=0 NormalY=0 NormalZ=1 AngleXU=0 Radius=8 StartAngle=4.71239 EndAngle=7.85398
    g2: LineSegment StartX=11 StartY=17 StartZ=0 EndX=26 EndY=17 EndZ=0
    g3: LineSegment StartX=26 StartY=33 StartZ=0 EndX=11 EndY=33 EndZ=0
    g4: ArcOfCircle CenterX=74 CenterY=25 CenterZ=0 NormalX=0 NormalY=0 NormalZ=1 AngleXU=0 Radius=8 StartAngle=1.5708 EndAngle=4.71239
    g5: ArcOfCircle CenterX=89 CenterY=25 CenterZ=0 NormalX=0 NormalY=0 NormalZ=1 AngleXU=0 Radius=8 StartAngle=4.71239 EndAngle=7.85398
    g6: LineSegment StartX=74 StartY=17 StartZ=0 EndX=89 EndY=17 EndZ=0
    g7: LineSegment StartX=89 StartY=33 StartZ=0 EndX=74 EndY=33 EndZ=0
    g8: LineSegment [constr] StartX=50 StartY=50 StartZ=0 EndX=50 EndY=0 EndZ=0
    g9: LineSegment [constr] StartX=0 StartY=25 StartZ=0 EndX=100 EndY=25 EndZ=0
  constraints (26):
    c: Tangent(g0,g2) = -1.5708
    c: Tangent(g2,g1) = -1.5708
    c: Tangent(g1,g3) = -1.5708
    c: Tangent(g3,g0) = -1.5708
    c: Equal(g0,g1)
    c: Tangent(g4,g6) = -1.5708
    c: Tangent(g6,g5) = -1.5708
    c: Tangent(g5,g7) = -1.5708
    c: Tangent(g7,g4) = -1.5708
    c: Equal(g4,g5)
    c: PointOnObject(g-7,g9)
    c: PointOnObject(g-7,g8)
    c: PointOnObject(g8,g-6)
    c: PointOnObject(g8,g-5)
    c: PointOnObject(g9,g-3)
    c: PointOnObject(g9,g-4)
    c: Horizontal(g9)
    c: Vertical(g8)
    c: PointOnObject(g0,g9)
    c: PointOnObject(g1,g9)
    c: Symmetric(g1,g4,g8)
    c: Symmetric(g5,g0,g8)
    c: Equal(g1,g4)
    c: DistanceX(g-3,g0) = 11
    c: DistanceX(g1,g8) = 24
    c: DistanceY(g-7,g1) = 8
FEATURE [PartDesign::Pocket] Pocket109
  BaseFeature = -> Pocket108
  Direction = (0,0,-1)
  Length = 5
  Length2 = 100
  Profile = -> Sketch257
  Suppressed = false
  Type = 1
FEATURE [Sketcher::SketchObject] Sketch258
  ArcFitTolerance = 0
  AttachmentSupport = -> [Pocket109]
  ExternalGeometry = -> [Pocket109]
  FullyConstrained = true
  MakeInternals = false
  MapMode = 5
  Placement = pos=(0,0,4) rot=(0,0,1;0rad)
  sketch-geometry (4):
    g0: Circle CenterX=29 CenterY=41 CenterZ=0 NormalX=0 NormalY=0 NormalZ=1 AngleXU=0 Radius=3.5
    g1: Circle CenterX=71 CenterY=41 CenterZ=0 NormalX=0 NormalY=0 NormalZ=1 AngleXU=0 Radius=3.5
    g2: Circle CenterX=29 CenterY=9 CenterZ=0 NormalX=0 NormalY=0 NormalZ=1 AngleXU=0 Radius=3.5
    g3: Circle CenterX=71 CenterY=9 CenterZ=0 NormalX=0 NormalY=0 NormalZ=1 AngleXU=0 Radius=3.5
  constraints (8):
    c: Coincident(g-3,g0)
    c: Coincident(g1,g-4)
    c: Coincident(g2,g-5)
    c: Coincident(g3,g-6)
    c: Equal(g0,g1)
    c: Equal(g0,g2)
    c: Equal(g0,g3)
    c: Diameter(g0) = 7
FEATURE [PartDesign::Pocket] Pocket110
  BaseFeature = -> Pocket109
  Direction = (0,0,-1)
  Length = 2
  Length2 = 100
  Profile = -> Sketch258
  Suppressed = false
  Type = 0
FEATURE [PartDesign::Body] Body087  label="pince_support_cremaillere001"
  AllowCompound = false
  Group = -> [Sketch255,Pad122,Sketch256,Pocket108,Sketch257,Pocket109,Sketch258,Pocket110]
  Origin = -> Origin288
  Placement = pos=(-25,-5,20) rot=(0,0,1;0rad)
  Tip = -> Pocket110
COMPONENT P7 — recipe-attached ("mousse002", modeled in this document).
Construction recipe (the document's own serialized feature program — sketch geometry with constraints, then the solid features built on it; lengths are millimeters unless a unit is written):

FEATURE [Sketcher::SketchObject] Sketch259
  ArcFitTolerance = 1e-06
  AttachmentSupport = -> [XZ_Plane286]
  FullyConstrained = true
  MakeInternals = false
  MapMode = 5
  Placement = pos=(0,0,0) rot=(1,0,0;1.5708rad)
  sketch-geometry (4):
    g0: LineSegment StartX=-4.5 StartY=0 StartZ=0 EndX=4.5 EndY=0 EndZ=0
    g1: LineSegment StartX=4.5 StartY=0 StartZ=0 EndX=4.5 EndY=3 EndZ=0
    g2: LineSegment StartX=4.5 StartY=3 StartZ=0 EndX=-4.5 EndY=3 EndZ=0
    g3: LineSegment StartX=-4.5 StartY=3 StartZ=0 EndX=-4.5 EndY=0 EndZ=0
  constraints (11):
    c: Coincident(g0,g1)
    c: Coincident(g1,g2)
    c: Coincident(g2,g3)
    c: Coincident(g3,g0)
    c: Horizontal(g0)
    c: Vertical(g1)
    c: Vertical(g3)
    c: PointOnObject(g0,g-1)
    c: Symmetric(g1,g2,g-2)
    c: Distance(g2,g2) = 9
    c: DistanceY(g3,g3) = 3
FEATURE [PartDesign::Pad] Pad123
  Direction = (0,-1,2e-16)
  Length = 40
  Length2 = 10
  Midplane = true
  Placement = pos=(0,0,0) rot=(1,0,0;1.5708rad)
  Profile = -> Sketch259
  ReferenceAxis = -> Sketch259 [N_Axis]
  Suppressed = false
  Type = 0
FEATURE [PartDesign::Body] Body088  label="mousse002"
  AllowCompound = false
  Group = -> [Sketch259,Pad123]
  Origin = -> Origin289
  Placement = pos=(71.5056,23,59.5) rot=(0.707107,0,0.707107;3.14159rad)
  Tip = -> Pad123
COMPONENT P8 — recipe-attached ("support_rail_haut001", modeled in this document).
Construction recipe (the document's own serialized feature program — sketch geometry with constraints, then the solid features built on it; lengths are millimeters unless a unit is written):

FEATURE [Sketcher::SketchObject] Sketch263
  ArcFitTolerance = 1e-06
  AttachmentSupport = -> [YZ_Plane289]
  FullyConstrained = true
  MakeInternals = false
  MapMode = 5
  Placement = pos=(0,0,0) rot=(0.57735,0.57735,0.57735;2.0944rad)
  sketch-geometry (20):
    g0: LineSegment StartX=-16.6 StartY=41.5 StartZ=0 EndX=-16.6 EndY=39.5 EndZ=0
    g1: LineSegment StartX=-14.6 StartY=37.5 StartZ=0 EndX=-8.6 EndY=37.5 EndZ=0
    g2: LineSegment StartX=-6.6 StartY=35.5 StartZ=0 EndX=-6.6 EndY=-4.1 EndZ=0
    g3: LineSegment StartX=-4.6 StartY=-6.1 StartZ=0 EndX=0 EndY=-6.1 EndZ=0
    g4: LineSegment StartX=0 StartY=-6.1 StartZ=0 EndX=0 EndY=-0.1 EndZ=0
    g5: LineSegment StartX=0 StartY=-0.1 StartZ=0 EndX=-4.6 EndY=-0.1 EndZ=0
    g6: LineSegment StartX=-4.6 StartY=-0.1 StartZ=0 EndX=-4.6 EndY=6.6 EndZ=0
    g7: LineSegment StartX=-4.6 StartY=6.6 StartZ=0 EndX=0 EndY=6.6 EndZ=0
    g8: LineSegment StartX=0 StartY=6.6 StartZ=0 EndX=0 EndY=41.5 EndZ=0
    g9: LineSegment StartX=0 StartY=41.5 StartZ=0 EndX=-16.6 EndY=41.5 EndZ=0
    g10: ArcOfCircle CenterX=-8.6 CenterY=35.5 CenterZ=0 NormalX=0 NormalY=0 NormalZ=1 AngleXU=0 Radius=2 StartAngle=0 EndAngle=1.5708
    g11: GeomPoint [constr] X=-6.6 Y=37.5 Z=0
    g12: ArcOfCircle CenterX=-4.6 CenterY=-4.1 CenterZ=0 NormalX=0 NormalY=0 NormalZ=1 AngleXU=0 Radius=2 StartAngle=3.14159 EndAngle=4.71239
    g13: GeomPoint [constr] X=-6.6 Y=-6.1 Z=0
    g14: ArcOfCircle CenterX=-14.6 CenterY=39.5 CenterZ=0 NormalX=0 NormalY=0 NormalZ=1 AngleXU=0 Radius=2 StartAngle=3.14159 EndAngle=4.71239
    g15: GeomPoint [constr] X=-16.6 Y=37.5 Z=0
    g16: LineSegment [constr] StartX=-4.5 StartY=6.5 StartZ=0 EndX=-4.5 EndY=0 EndZ=0
    g17: LineSegment [constr] StartX=-4.5 StartY=0 StartZ=0 EndX=0 EndY=0 EndZ=0
    g18: LineSegment [constr] StartX=0 StartY=0 StartZ=0 EndX=0 EndY=6.5 EndZ=0
    g19: LineSegment [constr] StartX=0 StartY=6.5 StartZ=0 EndX=-4.5 EndY=6.5 EndZ=0
  constraints (53):
    c: Vertical(g0)
    c: Horizontal(g1)
    c: Vertical(g2)
    c: PointOnObject(g3,g-2)
    c: Horizontal(g3)
    c: Coincident(g3,g4)
    c: PointOnObject(g4,g-2)
    c: Coincident(g4,g5)
    c: Horizontal(g5)
    c: Vertical(g6)
    c: Coincident(g6,g7)
    c: Horizontal(g7)
    c: Coincident(g7,g8)
    c: Vertical(g8)
    c: Coincident(g8,g9)
    c: Coincident(g9,g0)
    c: Horizontal(g9)
    c: PointOnObject(g7,g-2)
    c: PointOnObject(g11,g1)
    c: PointOnObject(g11,g2)
    c: Tangent(g1,g10) = 1.5708
    c: Tangent(g2,g10) = 1.5708
    c: PointOnObject(g13,g3)
    c: PointOnObject(g13,g2)
    c: Tangent(g3,g12) = -1.5708
    c: Tangent(g2,g12) = -1.5708
    c: PointOnObject(g15,g1)
    c: PointOnObject(g15,g0)
    c: Tangent(g1,g14) = -1.5708
    c: Tangent(g0,g14) = -1.5708
    c: DistanceY(g1,g0) = 4
    c: DistanceX(g0,g2) = 10
    c: Equal(g14,g10)
    c: Radius(g14) = 2
    c: Coincident(g16,g17)
    c: Coincident(g17,g18)
    c: Coincident(g18,g19)
    c: Coincident(g19,g16)
    c: Vertical(g16)
    c: Vertical(g18)
    c: Horizontal(g17)
    c: Horizontal(g19)
    c: Coincident(g17,g-1)
    c: DistanceX(g6,g16) = 0.1
    c: DistanceY(g18,g7) = 0.1
    c: DistanceX(g17,g17) = 4.5
    c: DistanceY(g18,g18) = 6.5
    c: DistanceY(g-1,g8) = 41.5
    c: DistanceY(g4,g4) = 6
    c: DistanceY(g4,g17) = 0.1
    c: Coincident(g5,g6)
    c: Vertical(g12,g5)
    c: Radius(g12) = 2
FEATURE [PartDesign::Pad] Pad125
  Direction = (1,0,0)
  Length = 20
  Length2 = 10
  Midplane = true
  Placement = pos=(0,0,0) rot=(1,1,1;2.0944rad)
  Profile = -> Sketch263
  ReferenceAxis = -> Sketch263 [N_Axis]
  Suppressed = false
  Type = 0
FEATURE [Sketcher::SketchObject] Sketch264
  ArcFitTolerance = 1e-06
  AttachmentSupport = -> [XY_Plane289]
  ExternalGeometry = -> [Pad125]
  FullyConstrained = true
  MakeInternals = false
  MapMode = 5
  Placement = pos=(0,0,0) rot=(0,1,0;3.14159rad)
  sketch-geometry (8):
    g0: Circle CenterX=0 CenterY=-11.6 CenterZ=0 NormalX=0 NormalY=0 NormalZ=1 AngleXU=0 Radius=2.75
    g1: LineSegment [constr] StartX=-5e-16 StartY=-8.6 StartZ=0 EndX=5e-16 EndY=-14.6 EndZ=0
    g2: LineSegment [constr] StartX=4 StartY=-9.6 StartZ=0 EndX=4 EndY=-16.6 EndZ=0
    g3: LineSegment [constr] StartX=4 StartY=-16.6 StartZ=0 EndX=10 EndY=-16.6 EndZ=0
    g4: LineSegment [constr] StartX=10 StartY=-16.6 StartZ=0 EndX=10 EndY=-8.6 EndZ=0
    g5: LineSegment [constr] StartX=10 StartY=-8.6 StartZ=0 EndX=5 EndY=-8.6 EndZ=0
    g6: ArcOfCircle [constr] CenterX=5 CenterY=-9.6 CenterZ=0 NormalX=0 NormalY=0 NormalZ=1 AngleXU=0 Radius=1 StartAngle=1.5708 EndAngle=3.14159
    g7: GeomPoint [constr] X=4 Y=-8.6 Z=0
  constraints (21):
    c: PointOnObject(g1,g-3)
    c: PointOnObject(g1,g-4)
    c: Perpendicular(g-3,g1)
    c: Symmetric(g1,g1,g0)
    c: Diameter(g0) = 5.5
    c: Coincident(g2,g3)
    c: Coincident(g3,g4)
    c: Coincident(g4,g5)
    c: Vertical(g2)
    c: Vertical(g4)
    c: Horizontal(g3)
    c: Horizontal(g5)
    c: Coincident(g3,g-5)
    c: PointOnObject(g7,g5)
    c: PointOnObject(g7,g2)
    c: Tangent(g5,g6) = -1.5708
    c: Tangent(g2,g6) = -1.5708
    c: PointOnObject(g7,g-3)
    c: Radius(g6) = 1
    c: DistanceX(g0,g2) = 4
    c: PointOnObject(g0,g-2)
FEATURE [PartDesign::Pocket] Pocket112
  BaseFeature = -> Pad125
  Direction = (0,0,1)
  Length = 5
  Length2 = 5
  Placement = pos=(0,0,0) rot=(1,1,1;2.0944rad)
  Profile = -> Sketch264
  ReferenceAxis = -> Sketch264 [N_Axis]
  Suppressed = false
  Type = 1
FEATURE [Sketcher::SketchObject] Sketch265
  ArcFitTolerance = 1e-06
  AttachmentOffset = pos=(0,0,-6) rot=(0,0,1;0rad)
  AttachmentSupport = -> [Pocket112]
  FullyConstrained = true
  MakeInternals = false
  MapMode = 5
  Placement = pos=(0,-1.3e-15,-0.1) rot=(0.707107,0.707107,0;3.14159rad)
  sketch-geometry (1):
    g0: Circle CenterX=0 CenterY=-3.5 CenterZ=0 NormalX=0 NormalY=0 NormalZ=1 AngleXU=0 Radius=2.1
  constraints (3):
    c: Diameter(g0) = 4.2
    c: PointOnObject(g0,g-2)
    c: DistanceY(g0,g-1) = 3.5
FEATURE [PartDesign::Pocket] Pocket113
  BaseFeature = -> Pocket112
  Direction = (0,0,1)
  Length = 16
  Length2 = 5
  Placement = pos=(0,0,0) rot=(1,1,1;2.0944rad)
  Profile = -> Sketch265
  ReferenceAxis = -> Sketch265 [N_Axis]
  Reversed = true
  Suppressed = false
  Type = 0
FEATURE [Sketcher::SketchObject] Sketch266
  ArcFitTolerance = 1e-06
  AttachmentSupport = -> [XZ_Plane289]
  ExternalGeometry = -> [Pocket113]
  FullyConstrained = true
  MakeInternals = false
  MapMode = 5
  Placement = pos=(0,0,0) rot=(1,0,0;1.5708rad)
  sketch-geometry (6):
    g0: LineSegment StartX=10 StartY=-6.1 StartZ=0 EndX=10 EndY=35.5 EndZ=0
    g1: LineSegment StartX=10 StartY=35.5 StartZ=0 EndX=2 EndY=-6.1 EndZ=0
    g2: LineSegment StartX=2 StartY=-6.1 StartZ=0 EndX=10 EndY=-6.1 EndZ=0
    g3: LineSegment StartX=-8 StartY=35 StartZ=0 EndX=4.5 EndY=22.5 EndZ=0
    g4: LineSegment StartX=4.5 StartY=22.5 StartZ=0 EndX=-8 EndY=10 EndZ=0
    g5: LineSegment StartX=-8 StartY=35 StartZ=0 EndX=-8 EndY=10 EndZ=0
  constraints (16):
    c: Coincident(g1,g2)
    c: Coincident(g2,g0)
    c: Horizontal(g2)
    c: Coincident(g0,g-4)
    c: Coincident(g0,g-3)
    c: Coincident(g0,g1)
    c: DistanceX(g2,g2) = 8
    c: Coincident(g4,g3)
    c: Coincident(g5,g3)
    c: Coincident(g5,g4)
    c: Vertical(g5)
    c: Angle(g5,g3) = 0.785398
    c: Equal(g3,g4)
    c: DistanceX(g3,g-1) = 8
    c: DistanceY(g-1,g3) = 35
    c: DistanceY(g5,g5) = 25
FEATURE [PartDesign::Pocket] Pocket114
  BaseFeature = -> Pocket113
  Direction = (0,1,-2e-16)
  Length = 5
  Length2 = 5
  Midplane = true
  Placement = pos=(0,0,0) rot=(1,1,1;2.0944rad)
  Profile = -> Sketch266
  ReferenceAxis = -> Sketch266 [N_Axis]
  Suppressed = false
  Type = 1
FEATURE [PartDesign::Mirrored] Mirrored011
  BaseFeature = -> Pocket114
  MirrorPlane = -> XZ_Plane289
  Originals = -> [Pocket114]
  Placement = pos=(0,0,0) rot=(1,1,1;2.0944rad)
  Refine = true
  Suppressed = false
  TransformMode = 1
FEATURE [Sketcher::SketchObject] Sketch
  ArcFitTolerance = 1e-06
  AttachmentSupport = -> [Mirrored011]
  FullyConstrained = true
  MakeInternals = false
  MapMode = 5
  Placement = pos=(0,-5.3e-15,6.6) rot=(0.707107,0.707107,0;3.14159rad)
  sketch-geometry (1):
    g0: Circle CenterX=0 CenterY=-3.5 CenterZ=0 NormalX=0 NormalY=0 NormalZ=1 AngleXU=0 Radius=3.25
  constraints (3):
    c: Diameter(g0) = 6.5
    c: PointOnObject(g0,g-2)
    c: DistanceY(g0,g-1) = 3.5
FEATURE [PartDesign::Pocket] Pocket
  BaseFeature = -> Mirrored011
  Direction = (0,0,1)
  Length = 5
  Length2 = 5
  Placement = pos=(0,0,0) rot=(1,1,1;2.0944rad)
  Profile = -> Sketch
  ReferenceAxis = -> Sketch [N_Axis]
  Suppressed = false
  Type = 1
FEATURE [PartDesign::Body] Body089  label="support_rail_haut001"
  AllowCompound = false
  Group = -> [Sketch263,Pad125,Sketch264,Pocket112,Sketch265,Pocket113,Sketch266,Pocket114,Mirrored011,Sketch,Pocket]
  Origin = -> Origin292
  Placement = pos=(0,-2e-15,218) rot=(-0.707107,0,-0.707107;3.14159rad)
  Tip = -> Pocket
COMPONENT P9 — recipe-attached ("cale", modeled in this document).
Construction recipe (the document's own serialized feature program — sketch geometry with constraints, then the solid features built on it; lengths are millimeters unless a unit is written):

FEATURE [Sketcher::SketchObject] Sketch267
  ArcFitTolerance = 1e-06
  AttachmentSupport = -> [XZ_Plane290]
  FullyConstrained = true
  MakeInternals = false
  MapMode = 5
  Placement = pos=(0,0,0) rot=(1,0,0;1.5708rad)
  sketch-geometry (4):
    g0: LineSegment StartX=-4.5 StartY=0 StartZ=0 EndX=4.5 EndY=0 EndZ=0
    g1: LineSegment StartX=4.5 StartY=0 StartZ=0 EndX=4.5 EndY=2 EndZ=0
    g2: LineSegment StartX=4.5 StartY=2 StartZ=0 EndX=-4.5 EndY=2 EndZ=0
    g3: LineSegment StartX=-4.5 StartY=2 StartZ=0 EndX=-4.5 EndY=0 EndZ=0
  constraints (11):
    c: Coincident(g0,g1)
    c: Coincident(g1,g2)
    c: Coincident(g2,g3)
    c: Coincident(g3,g0)
    c: Horizontal(g0)
    c: Vertical(g1)
    c: Vertical(g3)
    c: PointOnObject(g0,g-1)
    c: Symmetric(g1,g2,g-2)
    c: Distance(g2,g2) = 9
    c: DistanceY(g3,g3) = 2
FEATURE [PartDesign::Pad] Pad126
  Direction = (0,-1,2e-16)
  Length = 40
  Length2 = 10
  Midplane = true
  Placement = pos=(0,0,0) rot=(1,0,0;1.5708rad)
  Profile = -> Sketch267
  ReferenceAxis = -> Sketch267 [N_Axis]
  Suppressed = false
  Type = 0
FEATURE [PartDesign::Body] Body090  label="cale"
  AllowCompound = false
  Group = -> [Sketch267,Pad126]
  Origin = -> Origin293
  Placement = pos=(71.5056,23,59.5) rot=(0.707107,0,0.707107;3.14159rad)
  Tip = -> Pad126
COMPONENT P10 — recipe-attached ("porte_cale", modeled in this document).
Construction recipe (the document's own serialized feature program — sketch geometry with constraints, then the solid features built on it; lengths are millimeters unless a unit is written):

FEATURE [Sketcher::SketchObject] Sketch215
  ArcFitTolerance = 1e-06
  AttachmentSupport = -> [XY_Plane291]
  FullyConstrained = true
  MakeInternals = false
  MapMode = 5
  expr: Constraints[2] = 16.5 mm / 2
  sketch-geometry (5):
    g0: Circle CenterX=-8.25 CenterY=0 CenterZ=0 NormalX=0 NormalY=0 NormalZ=1 AngleXU=0 Radius=2.1
    g1: ArcOfCircle CenterX=-8.25 CenterY=0 CenterZ=0 NormalX=0 NormalY=0 NormalZ=1 AngleXU=0 Radius=3 StartAngle=1.5708 EndAngle=4.71239
    g2: LineSegment StartX=0 StartY=-3 StartZ=0 EndX=-8.25 EndY=-3 EndZ=0
    g3: LineSegment StartX=0 StartY=3 StartZ=0 EndX=-8.25 EndY=3 EndZ=0
    g4: LineSegment StartX=0 StartY=3 StartZ=0 EndX=0 EndY=-3 EndZ=0
  constraints (13):
    c: Diameter(g0) = 4.2
    c: PointOnObject(g0,g-1)
    c: DistanceX(g0,g-1) = 8.25
    c: Tangent(g1,g2) = 1.5708
    c: Tangent(g1,g3) = -1.5708
    c: Horizontal(g3)
    c: Coincident(g1,g0)
    c: PointOnObject(g3,g-2)
    c: PointOnObject(g2,g-2)
    c: Coincident(g4,g3)
    c: Coincident(g4,g2)
    c: Horizontal(g2)
    c: Radius(g1) = 3
FEATURE [PartDesign::Pad] Pad110
  Direction = (0,0,1)
  Length = 15
  Length2 = 10
  Profile = -> Sketch215
  ReferenceAxis = -> Sketch215 [N_Axis]
  Suppressed = false
  Type = 0
FEATURE [Sketcher::SketchObject] Sketch216
  ArcFitTolerance = 1e-06
  AttachmentSupport = -> [XZ_Plane291]
  FullyConstrained = true
  MakeInternals = false
  MapMode = 5
  Placement = pos=(0,0,0) rot=(1,0,0;1.5708rad)
  sketch-geometry (6):
    g0: LineSegment StartX=-3.2536 StartY=15 StartZ=0 EndX=-3.11715 EndY=7.18255 EndZ=0
    g1: LineSegment StartX=0 StartY=6.2 StartZ=0 EndX=-2.1173 EndY=6.2 EndZ=0
    g2: LineSegment StartX=0 StartY=6.2 StartZ=0 EndX=0 EndY=15 EndZ=0
    g3: LineSegment StartX=-3.2536 StartY=15 StartZ=0 EndX=0 EndY=15 EndZ=0
    g4: ArcOfCircle CenterX=-2.1173 CenterY=7.2 CenterZ=0 NormalX=0 NormalY=0 NormalZ=1 AngleXU=0 Radius=1 StartAngle=3.15905 EndAngle=4.71239
    g5: GeomPoint [constr] X=-3.1 Y=6.2 Z=0
  constraints (16):
    c: PointOnObject(g1,g-2)
    c: Coincident(g2,g1)
    c: Vertical(g2)
    c: Coincident(g3,g0)
    c: Coincident(g3,g2)
    c: DistanceY(g-1,g1) = 6.2
    c: Horizontal(g3)
    c: DistanceY(g-1,g0) = 15
    c: Horizontal(g1)
    c: DistanceX(g5,g1) = 3.1
    c: PointOnObject(g5,g0)
    c: PointOnObject(g5,g1)
    c: Tangent(g0,g4) = -1.5708
    c: Tangent(g1,g4) = 1.5708
    c: Angle(g1,g0) = 1.58825
    c: Radius(g4) = 1
FEATURE [PartDesign::Pocket] Pocket079
  BaseFeature = -> Pad110
  Direction = (0,1,-2e-16)
  Length = 5
  Length2 = 5
  Midplane = true
  Profile = -> Sketch216
  ReferenceAxis = -> Sketch216 [N_Axis]
  Suppressed = false
  Type = 1
FEATURE [Sketcher::SketchObject] Sketch268
  ArcFitTolerance = 1e-06
  AttachmentSupport = -> [XZ_Plane291]
  ExternalGeometry = -> [Pocket079]
  FullyConstrained = true
  MakeInternals = false
  MapMode = 5
  Placement = pos=(0,0,0) rot=(1,0,0;1.5708rad)
  sketch-geometry (3):
    g0: LineSegment StartX=-12 StartY=8 StartZ=0 EndX=-5 EndY=15 EndZ=0
    g1: LineSegment StartX=-12 StartY=15 StartZ=0 EndX=-12 EndY=8 EndZ=0
    g2: LineSegment StartX=-5 StartY=15 StartZ=0 EndX=-12 EndY=15 EndZ=0
  constraints (9):
    c: Vertical(g1)
    c: Coincident(g1,g2)
    c: Coincident(g0,g2)
    c: Coincident(g0,g1)
    c: Horizontal(g2)
    c: Horizontal(g2,g-3)
    c: DistanceX(g1,g-1) = 12
    c: Angle(g0,g1) = 0.785398
    c: DistanceX(g2,g2) = 7
FEATURE [PartDesign::Pocket] Pocket115
  BaseFeature = -> Pocket079
  Direction = (0,1,-2e-16)
  Length = 5
  Length2 = 5
  Midplane = true
  Profile = -> Sketch268
  ReferenceAxis = -> Sketch268 [N_Axis]
  Suppressed = false
  Type = 1
FEATURE [PartDesign::Mirrored] Mirrored046
  BaseFeature = -> Pocket115
  MirrorPlane = -> Sketch216 [V_Axis]
  Originals = -> [Pocket079]
  Suppressed = false
  TransformMode = 1
FEATURE [PartDesign::Body] Body091  label="porte_cale"
  AllowCompound = false
  Group = -> [Sketch215,Pad110,Sketch216,Pocket079,Sketch268,Pocket115,Mirrored046]
  Origin = -> Origin294
  Placement = pos=(71.5,19.83,20) rot=(-0.707107,-0.707107,0;3.14159rad)
  Tip = -> Mirrored046
COMPONENT P11 — recipe-attached ("pince_capot002", modeled in this document).
Construction recipe (the document's own serialized feature program — sketch geometry with constraints, then the solid features built on it; lengths are millimeters unless a unit is written):

FEATURE [Sketcher::SketchObject] Sketch279
  ArcFitTolerance = 0
  AttachmentSupport = -> [XY_Plane369]
  FullyConstrained = true
  MakeInternals = false
  MapMode = 2
  sketch-geometry (31):
    g0: LineSegment StartX=0 StartY=50 StartZ=0 EndX=100 EndY=50 EndZ=0
    g1: LineSegment StartX=100 StartY=50 StartZ=0 EndX=100 EndY=48 EndZ=0
    g2: LineSegment StartX=100 StartY=0 StartZ=0 EndX=0 EndY=0 EndZ=0
    g3: LineSegment StartX=0 StartY=0 StartZ=0 EndX=0 EndY=2 EndZ=0
    g4: Circle CenterX=50 CenterY=25 CenterZ=0 NormalX=0 NormalY=0 NormalZ=1 AngleXU=0 Radius=14
    g5: LineSegment [constr] StartX=0 StartY=50 StartZ=0 EndX=100 EndY=0 EndZ=0
    g6: LineSegment [constr] StartX=0 StartY=0 StartZ=0 EndX=100 EndY=50 EndZ=0
    g7: LineSegment [constr] StartX=0 StartY=25 StartZ=0 EndX=100 EndY=25 EndZ=0
    g8: LineSegment [constr] StartX=50 StartY=50 StartZ=0 EndX=50 EndY=0 EndZ=0
    g9: LineSegment [constr] StartX=3.5 StartY=33.25 StartZ=0 EndX=96.5 EndY=33.25 EndZ=0
    g10: LineSegment [constr] StartX=96.5 StartY=33.25 StartZ=0 EndX=96.5 EndY=16.75 EndZ=0
    g11: LineSegment [constr] StartX=96.5 StartY=16.75 StartZ=0 EndX=3.5 EndY=16.75 EndZ=0
    g12: LineSegment [constr] StartX=3.5 StartY=16.75 StartZ=0 EndX=3.5 EndY=33.25 EndZ=0
    g13: Circle CenterX=96.5 CenterY=33.25 CenterZ=0 NormalX=0 NormalY=0 NormalZ=1 AngleXU=0 Radius=1.65
    g14: Circle CenterX=3.5 CenterY=33.25 CenterZ=0 NormalX=0 NormalY=0 NormalZ=1 AngleXU=0 Radius=1.65
    g15: Circle CenterX=3.5 CenterY=16.75 CenterZ=0 NormalX=0 NormalY=0 NormalZ=1 AngleXU=0 Radius=1.65
    g16: Circle CenterX=96.5 CenterY=16.75 CenterZ=0 NormalX=0 NormalY=0 NormalZ=1 AngleXU=0 Radius=1.65
    g17: LineSegment StartX=0 StartY=2 StartZ=0 EndX=30 EndY=2 EndZ=0
    g18: LineSegment StartX=30 StartY=2 StartZ=0 EndX=30 EndY=7.5 EndZ=0
    g19: LineSegment StartX=30 StartY=7.5 StartZ=0 EndX=2.5 EndY=7.5 EndZ=0
    g20: LineSegment StartX=0 StartY=10 StartZ=0 EndX=0 EndY=50 EndZ=0
    g21: LineSegment StartX=100 StartY=48 StartZ=0 EndX=67.5 EndY=48 EndZ=0
    g22: LineSegment StartX=67.5 StartY=48 StartZ=0 EndX=67.5 EndY=42.5 EndZ=0
    g23: LineSegment StartX=67.5 StartY=42.5 StartZ=0 EndX=97.5 EndY=42.5 EndZ=0
    g24: LineSegment StartX=100 StartY=40 StartZ=0 EndX=100 EndY=0 EndZ=0
    g25: ArcOfCircle [constr] CenterX=97.5 CenterY=40 CenterZ=0 NormalX=0 NormalY=0 NormalZ=1 AngleXU=0 Radius=2.5 StartAngle=0 EndAngle=1.5708
    g26: GeomPoint [constr] X=100 Y=42.5 Z=0
    g27: LineSegment StartX=100 StartY=40 StartZ=0 EndX=97.5 EndY=42.5 EndZ=0
    g28: ArcOfCircle [constr] CenterX=2.5 CenterY=10 CenterZ=0 NormalX=0 NormalY=0 NormalZ=1 AngleXU=0 Radius=2.5 StartAngle=3.14159 EndAngle=4.71239
    g29: GeomPoint [constr] X=0 Y=7.5 Z=0
    g30: LineSegment StartX=0 StartY=10 StartZ=0 EndX=2.5 EndY=7.5 EndZ=0
  constraints (78):
    c: Coincident(g0,g1)
    c: Coincident(g24,g2)
    c: Coincident(g2,g3)
    c: Coincident(g20,g0)
    c: Horizontal(g0)
    c: Horizontal(g2)
    c: Vertical(g1)
    c: Vertical(g3)
    c: Coincident(g2,g-1)
    c: Coincident(g5,g0)
    c: Coincident(g2,g6)
    c: Coincident(g0,g6)
    c: Coincident(g24,g5)
    c: PointOnObject(g4,g6)
    c: PointOnObject(g4,g5)
    c: Diameter(g4) = 28
    c: DistanceY(g3,g20) = 50
    c: DistanceX(g2,g2) = 100
    c: PointOnObject(g8,g0)
    c: PointOnObject(g7,g24)
    c: PointOnObject(g7,g20)
    c: PointOnObject(g8,g2)
    c: Symmetric(g0,g0,g8)
    c: Symmetric(g0,g2,g7)
    c: Coincident(g9,g10)
    c: Coincident(g10,g11)
    c: Coincident(g11,g12)
    c: Coincident(g12,g9)
    c: Horizontal(g11)
    c: Vertical(g12)
    c: Symmetric(g9,g10,g7)
    c: Symmetric(g9,g9,g8)
    c: Distance(g12) = 16.5
    c: DistanceX(g0,g9) = 3.5
    c: Coincident(g16,g10)
    c: Coincident(g13,g9)
    c: Coincident(g9,g14)
    c: Coincident(g11,g15)
    c: Equal(g14,g15)
    c: Equal(g14,g13)
    c: Equal(g14,g16)
    c: Diameter(g14) = 3.3
    c: Coincident(g17,g18)
    c: Coincident(g18,g19)
    c: Horizontal(g17)
    c: Horizontal(g19)
    c: Vertical(g18)
    c: Vertical(g20)
    c: DistanceX(g29,g19) = 30
    c: Coincident(g21,g22)
    c: Coincident(g22,g23)
    c: Horizontal(g21)
    c: Horizontal(g23)
    c: Vertical(g22)
    c: Vertical(g24)
    c: Equal(g18,g22)
    c: PointOnObject(g26,g23)
    c: PointOnObject(g26,g24)
    c: Tangent(g23,g25) = 1.5708
    c: Tangent(g24,g25) = 1.5708
    c: Coincident(g27,g23)
    c: Coincident(g27,g24)
    c: PointOnObject(g29,g20)
    c: PointOnObject(g29,g19)
    c: Tangent(g20,g28) = 1.5708
    c: Tangent(g19,g28) = 1.5708
    c: Coincident(g30,g20)
    c: Coincident(g30,g19)
    c: Equal(g1,g3)
    c: Equal(g23,g17)
    c: Coincident(g3,g17)
    c: DistanceY(g3,g3) = 2
    c: Coincident(g1,g21)
    c: Vertical(g1,g24)
    c: Vertical(g29,g3)
    c: DistanceY(g18,g18) = 5.5
    c: Radius(g28) = 2.5
    c: Equal(g25,g28)
FEATURE [PartDesign::Pad] Pad135
  AlongSketchNormal = false
  Direction = (0,0,1)
  Length = 4
  Length2 = 100
  Profile = -> Sketch279
  ReferenceAxis = -> Sketch279 [N_Axis]
  Suppressed = false
  Type = 0
FEATURE [Sketcher::SketchObject] Sketch280
  ArcFitTolerance = 1e-06
  AttachmentOffset = pos=(0,0,4) rot=(0,0,1;0rad)
  AttachmentSupport = -> [XY_Plane369]
  ExternalGeometry = -> [Pad135]
  FullyConstrained = true
  MakeInternals = false
  MapMode = 5
  Placement = pos=(0,0,4) rot=(0,0,1;0rad)
  sketch-geometry (4):
    g0: Circle CenterX=3.5 CenterY=33.25 CenterZ=0 NormalX=0 NormalY=0 NormalZ=1 AngleXU=0 Radius=3.25
    g1: Circle CenterX=3.5 CenterY=16.75 CenterZ=0 NormalX=0 NormalY=0 NormalZ=1 AngleXU=0 Radius=3.25
    g2: Circle CenterX=96.5 CenterY=33.25 CenterZ=0 NormalX=0 NormalY=0 NormalZ=1 AngleXU=0 Radius=3.25
    g3: Circle CenterX=96.5 CenterY=16.75 CenterZ=0 NormalX=0 NormalY=0 NormalZ=1 AngleXU=0 Radius=3.25
  constraints (10):
    c: Coincident(g0,g-3)
    c: Coincident(g1,g-4)
    c: Equal(g0,g1)
    c: Equal(g1,g2)
    c: Equal(g2,g3)
    c: Diameter(g0) = 6.5
    c: Horizontal(g3,g1)
    c: Horizontal(g2,g0)
    c: Vertical(g2,g3)
    c: DistanceX(g1,g3) = 93
FEATURE [PartDesign::Pocket] Pocket117
  BaseFeature = -> Pad135
  Direction = (0,0,-1)
  Length = 2
  Length2 = 5
  Profile = -> Sketch280
  ReferenceAxis = -> Sketch280 [N_Axis]
  Refine = true
  Suppressed = false
  Type = 0
FEATURE [PartDesign::Body] Body099  label="pince_capot002"
  AllowCompound = false
  Group = -> [Sketch279,Pad135,Sketch280,Pocket117]
  Origin = -> Origin372
  Placement = pos=(-25,-5,28) rot=(0,0,1;0rad)
  Tip = -> Pocket117
COMPONENT P12 — recipe-attached ("pince_cremaillere_bras004", modeled in this document).
Construction recipe (the document's own serialized feature program — sketch geometry with constraints, then the solid features built on it; lengths are millimeters unless a unit is written):

FEATURE [PartDesign::FeatureBase] BaseFeature004
  BaseFeature = -> InvoluteRack002
  Suppressed = false
FEATURE [Sketcher::SketchObject] Sketch281
  ArcFitTolerance = 1e-06
  AttachmentSupport = -> [BaseFeature004]
  FullyConstrained = true
  MakeInternals = false
  MapMode = 5
  Placement = pos=(0,92.677,0) rot=(0,0.707107,0.707107;3.14159rad)
  sketch-geometry (4):
    g0: LineSegment StartX=-29.25 StartY=0 StartZ=0 EndX=10.75 EndY=0 EndZ=0
    g1: LineSegment StartX=10.75 StartY=0 StartZ=0 EndX=10.75 EndY=40 EndZ=0
    g2: LineSegment StartX=10.75 StartY=40 StartZ=0 EndX=-29.25 EndY=40 EndZ=0
    g3: LineSegment StartX=-29.25 StartY=40 StartZ=0 EndX=-29.25 EndY=0 EndZ=0
  constraints (12):
    c: Coincident(g0,g1)
    c: Coincident(g1,g2)
    c: Coincident(g2,g3)
    c: Coincident(g3,g0)
    c: Horizontal(g0)
    c: Horizontal(g2)
    c: Vertical(g1)
    c: Vertical(g3)
    c: DistanceY(g3,g3) = 40
    c: DistanceX(g2,g2) = 40
    c: PointOnObject(g0,g-1)
    c: DistanceX(g-1,g0) = 10.75
FEATURE [PartDesign::Pad] Pad136
  BaseFeature = -> BaseFeature004
  Direction = (0,1,-2e-16)
  Length = 5
  Length2 = 10
  Profile = -> Sketch281
  ReferenceAxis = -> Sketch281 [N_Axis]
  Refine = true
  Suppressed = false
  Type = 0
FEATURE [Sketcher::SketchObject] Sketch299
  ArcFitTolerance = 1e-06
  AttachmentOffset = pos=(0,0,-10.75) rot=(0,0,1;0rad)
  AttachmentSupport = -> [YZ_Plane370]
  ExternalGeometry = -> [Pad136]
  FullyConstrained = true
  MakeInternals = false
  MapMode = 5
  Placement = pos=(-10.75,0,0) rot=(0.57735,0.57735,0.57735;2.0944rad)
  sketch-geometry (3):
    g0: LineSegment StartX=67.677 StartY=3 StartZ=0 EndX=92.677 EndY=9 EndZ=0
    g1: LineSegment StartX=67.677 StartY=3 StartZ=0 EndX=92.677 EndY=3 EndZ=0
    g2: LineSegment StartX=92.677 StartY=9 StartZ=0 EndX=92.677 EndY=3 EndZ=0
  constraints (8):
    c: PointOnObject(g0,g-4)
    c: Coincident(g1,g0)
    c: Coincident(g1,g-4)
    c: Coincident(g2,g0)
    c: Coincident(g2,g1)
    c: DistanceX(g1,g1) = 25
    c: Vertical(g2)
    c: DistanceY(g2,g2) = 6
FEATURE [PartDesign::Pad] Pad141
  BaseFeature = -> Pad136
  Direction = (1,0,0)
  Length = 5
  Length2 = 10
  Profile = -> Sketch299
  ReferenceAxis = -> Sketch299 [N_Axis]
  Suppressed = false
  Type = 0
FEATURE [PartDesign::Body] Body100  label="pince_cremaillere_bras004"
  AllowCompound = false
  BaseFeature = -> InvoluteRack002
  Group = -> [BaseFeature004,Sketch281,Pad136,Sketch299,Pad141]
  Origin = -> Origin373
  Placement = pos=(-18.1714,32.25,24) rot=(0,0,-1;1.5708rad)
  Tip = -> Pad141
COMPONENT P13 — recipe-attached ("pince_support_servo002", modeled in this document).
Construction recipe (the document's own serialized feature program — sketch geometry with constraints, then the solid features built on it; lengths are millimeters unless a unit is written):

FEATURE [Sketcher::SketchObject] Sketch282
  ArcFitTolerance = 0
  AttachmentOffset = pos=(0,0,-2) rot=(0,0,1;0rad)
  AttachmentSupport = -> [XY_Plane371]
  FullyConstrained = true
  MakeInternals = false
  MapMode = 2
  Placement = pos=(0,0,-2) rot=(0,0,1;0rad)
  sketch-geometry (18):
    g0: LineSegment StartX=14.5 StartY=50 StartZ=0 EndX=35.5 EndY=50 EndZ=0
    g1: LineSegment StartX=35.5 StartY=50 StartZ=0 EndX=35.5 EndY=9 EndZ=0
    g2: LineSegment StartX=35.5 StartY=9 StartZ=0 EndX=14.5 EndY=9 EndZ=0
    g3: LineSegment StartX=14.5 StartY=9 StartZ=0 EndX=14.5 EndY=50 EndZ=0
    g4: LineSegment StartX=0 StartY=59 StartZ=0 EndX=50 EndY=59 EndZ=0
    g5: LineSegment StartX=50 StartY=59 StartZ=0 EndX=50 EndY=0 EndZ=0
    g6: LineSegment StartX=50 StartY=0 StartZ=0 EndX=0 EndY=0 EndZ=0
    g7: LineSegment StartX=0 StartY=0 StartZ=0 EndX=0 EndY=59 EndZ=0
    g8: Circle CenterX=19 CenterY=54.5 CenterZ=0 NormalX=0 NormalY=0 NormalZ=1 AngleXU=0 Radius=1.65
    g9: Circle CenterX=31 CenterY=54.5 CenterZ=0 NormalX=0 NormalY=0 NormalZ=1 AngleXU=0 Radius=1.65
    g10: Circle CenterX=19 CenterY=4.5 CenterZ=0 NormalX=0 NormalY=0 NormalZ=1 AngleXU=0 Radius=1.65
    g11: Circle CenterX=31 CenterY=4.5 CenterZ=0 NormalX=0 NormalY=0 NormalZ=1 AngleXU=0 Radius=1.65
    g12: LineSegment [constr] StartX=19 StartY=54.5 StartZ=0 EndX=31 EndY=54.5 EndZ=0
    g13: LineSegment [constr] StartX=31 StartY=54.5 StartZ=0 EndX=31 EndY=4.5 EndZ=0
    g14: LineSegment [constr] StartX=31 StartY=4.5 StartZ=0 EndX=19 EndY=4.5 EndZ=0
    g15: LineSegment [constr] StartX=19 StartY=4.5 StartZ=0 EndX=19 EndY=54.5 EndZ=0
    g16: LineSegment [constr] StartX=14.5 StartY=29.5 StartZ=0 EndX=35.5 EndY=29.5 EndZ=0
    g17: LineSegment [constr] StartX=25 StartY=50 StartZ=0 EndX=25 EndY=9 EndZ=0
  constraints (46):
    c: Coincident(g0,g1)
    c: Coincident(g1,g2)
    c: Coincident(g2,g3)
    c: Coincident(g3,g0)
    c: Horizontal(g0)
    c: Horizontal(g2)
    c: Vertical(g1)
    c: Vertical(g3)
    c: Coincident(g4,g5)
    c: Coincident(g5,g6)
    c: Coincident(g6,g7)
    c: Coincident(g7,g4)
    c: Horizontal(g6)
    c: Vertical(g5)
    c: Coincident(g12,g13)
    c: Coincident(g13,g14)
    c: Coincident(g14,g15)
    c: Coincident(g15,g12)
    c: Horizontal(g14)
    c: Vertical(g15)
    c: Coincident(g10,g14)
    c: Coincident(g11,g13)
    c: Coincident(g8,g12)
    c: Coincident(g9,g12)
    c: PointOnObject(g17,g0)
    c: PointOnObject(g17,g2)
    c: PointOnObject(g16,g3)
    c: PointOnObject(g16,g1)
    c: Symmetric(g0,g0,g17)
    c: Symmetric(g2,g0,g16)
    c: Symmetric(g9,g8,g17)
    c: DistanceX(g2,g2) = 21
    c: DistanceY(g3,g3) = 41
    c: DistanceX(g14,g14) = 12
    c: DistanceY(g13,g13) = 50
    c: Equal(g9,g8)
    c: Equal(g9,g11)
    c: Equal(g9,g10)
    c: Diameter(g9) = 3.3
    c: Symmetric(g9,g11,g16)
    c: Coincident(g-1,g6)
    c: Symmetric(g4,g4,g17)
    c: DistanceX(g6,g2) = 14.5
    c: Vertical(g7)
    c: DistanceY(g5,g5) = 59
    c: DistanceY(g-1,g2) = 9
FEATURE [PartDesign::Pad] Pad137
  AlongSketchNormal = false
  Direction = (0,0,1)
  Length = 4
  Length2 = 100
  Profile = -> Sketch282
  ReferenceAxis = -> Sketch282 [N_Axis]
  Suppressed = false
  Type = 0
FEATURE [Sketcher::SketchObject] Sketch283
  ArcFitTolerance = 0
  AttachmentSupport = -> [Pad137]
  ExternalGeometry = -> [Pad137]
  FullyConstrained = true
  MakeInternals = false
  MapMode = 5
  Placement = pos=(0,0,2) rot=(0,0,1;0rad)
  sketch-geometry (10):
    g0: LineSegment StartX=0 StartY=40 StartZ=0 EndX=8 EndY=40 EndZ=0
    g1: LineSegment StartX=8 StartY=40 StartZ=0 EndX=8 EndY=0 EndZ=0
    g2: LineSegment StartX=8 StartY=0 StartZ=0 EndX=0 EndY=0 EndZ=0
    g3: LineSegment StartX=0 StartY=0 StartZ=0 EndX=0 EndY=40 EndZ=0
    g4: LineSegment StartX=42 StartY=40 StartZ=0 EndX=50 EndY=40 EndZ=0
    g5: LineSegment StartX=50 StartY=40 StartZ=0 EndX=50 EndY=0 EndZ=0
    g6: LineSegment StartX=50 StartY=0 StartZ=0 EndX=42 EndY=0 EndZ=0
    g7: LineSegment StartX=42 StartY=0 StartZ=0 EndX=42 EndY=40 EndZ=0
    g8: LineSegment [constr] StartX=25 StartY=59 StartZ=0 EndX=25 EndY=0 EndZ=0
    g9: LineSegment [constr] StartX=0 StartY=20 StartZ=0 EndX=50 EndY=20 EndZ=0
  constraints (28):
    c: Coincident(g0,g1)
    c: Coincident(g1,g2)
    c: Coincident(g2,g3)
    c: Coincident(g3,g0)
    c: Horizontal(g0)
    c: Horizontal(g2)
    c: Vertical(g3)
    c: Coincident(g4,g5)
    c: Coincident(g5,g6)
    c: Coincident(g6,g7)
    c: Coincident(g7,g4)
    c: Horizontal(g4)
    c: Horizontal(g6)
    c: Vertical(g5)
    c: PointOnObject(g4,g-4)
    c: PointOnObject(g8,g-5)
    c: PointOnObject(g8,g-6)
    c: Symmetric(g-5,g-5,g8)
    c: Symmetric(g0,g4,g8)
    c: DistanceX(g0,g0) = 8
    c: Vertical(g1)
    c: PointOnObject(g9,g3)
    c: PointOnObject(g9,g5)
    c: Symmetric(g0,g1,g9)
    c: Vertical(g7)
    c: PointOnObject(g5,g-1)
    c: DistanceY(g3,g3) = 40
    c: Coincident(g2,g-1)
FEATURE [PartDesign::Pad] Pad138
  AlongSketchNormal = false
  BaseFeature = -> Pad137
  Direction = (0,0,1)
  Length = 18
  Length2 = 100
  Profile = -> Sketch283
  Suppressed = false
  Type = 0
FEATURE [Sketcher::SketchObject] Sketch284
  ArcFitTolerance = 0
  AttachmentSupport = -> [Pad138]
  ExternalGeometry = -> [Pad138]
  FullyConstrained = true
  MakeInternals = false
  MapMode = 5
  Placement = pos=(0,0,20) rot=(0,0,1;0rad)
  sketch-geometry (7):
    g0: LineSegment [constr] StartX=25 StartY=40 StartZ=0 EndX=25 EndY=0 EndZ=0
    g1: LineSegment [constr] StartX=0 StartY=20 StartZ=0 EndX=50 EndY=20 EndZ=0
    g2: Circle CenterX=4 CenterY=36 CenterZ=0 NormalX=0 NormalY=0 NormalZ=1 AngleXU=0 Radius=1.75
    g3: Circle CenterX=46 CenterY=36 CenterZ=0 NormalX=0 NormalY=0 NormalZ=1 AngleXU=0 Radius=1.75
    g4: Circle CenterX=4 CenterY=4 CenterZ=0 NormalX=0 NormalY=0 NormalZ=1 AngleXU=0 Radius=1.75
    g5: Circle CenterX=46 CenterY=4 CenterZ=0 NormalX=0 NormalY=0 NormalZ=1 AngleXU=0 Radius=1.75
    g6: LineSegment [constr] StartX=4 StartY=36 StartZ=0 EndX=4 EndY=4 EndZ=0
  constraints (17):
    c: PointOnObject(g0,g-4)
    c: PointOnObject(g0,g-5)
    c: PointOnObject(g1,g-7)
    c: PointOnObject(g1,g-8)
    c: Symmetric(g-3,g-4,g0)
    c: Symmetric(g-5,g-4,g1)
    c: Symmetric(g4,g2,g1)
    c: Symmetric(g3,g2,g0)
    c: Symmetric(g5,g3,g1)
    c: Equal(g2,g4)
    c: Equal(g2,g3)
    c: Equal(g2,g5)
    c: Radius(g2) = 1.75
    c: Coincident(g6,g4)
    c: Coincident(g6,g2)
    c: Symmetric(g-7,g-5,g6)
    c: DistanceY(g-5,g4) = 4
FEATURE [PartDesign::Pocket] Pocket118
  BaseFeature = -> Pad138
  Direction = (0,0,-1)
  Length = 5
  Length2 = 100
  Profile = -> Sketch284
  Suppressed = false
  Type = 1
FEATURE [Sketcher::SketchObject] Sketch285
  ArcFitTolerance = 0
  AttachmentSupport = -> [Pocket118]
  ExternalGeometry = -> [Pocket118]
  FullyConstrained = true
  MakeInternals = false
  MapMode = 5
  Placement = pos=(50,0,0) rot=(0.57735,0.57735,0.57735;2.0944rad)
  sketch-geometry (7):
    g0: LineSegment [constr] StartX=0 StartY=20 StartZ=0 EndX=40 EndY=0 EndZ=0
    g1: LineSegment [constr] StartX=0 StartY=0 StartZ=0 EndX=40 EndY=20 EndZ=0
    g2: Circle CenterX=12 CenterY=17 CenterZ=0 NormalX=0 NormalY=0 NormalZ=1 AngleXU=0 Radius=1.75
    g3: Circle CenterX=12 CenterY=3 CenterZ=0 NormalX=0 NormalY=0 NormalZ=1 AngleXU=0 Radius=1.75
    g4: Circle CenterX=28 CenterY=3 CenterZ=0 NormalX=0 NormalY=0 NormalZ=1 AngleXU=0 Radius=1.75
    g5: Circle CenterX=28 CenterY=17 CenterZ=0 NormalX=0 NormalY=0 NormalZ=1 AngleXU=0 Radius=1.75
    g6: GeomPoint X=20 Y=10 Z=0
  constraints (19):
    c: Equal(g3,g2)
    c: Equal(g3,g5)
    c: Equal(g3,g4)
    c: Coincident(g0,g-5)
    c: Coincident(g1,g-4)
    c: DistanceX(g-3,g-3) = 40
    c: Horizontal(g2,g5)
    c: Horizontal(g3,g4)
    c: Diameter(g3) = 3.5
    c: Vertical(g3,g2)
    c: Vertical(g5,g4)
    c: PointOnObject(g6,g0)
    c: PointOnObject(g6,g1)
    c: DistanceX(g2,g6) = 8
    c: DistanceY(g6,g2) = 7
    c: Symmetric(g2,g4,g6)
    c: Coincident(g1,g-1)
    c: PointOnObject(g0,g-1)
    c: Vertical(g-4,g0)
FEATURE [PartDesign::Pocket] Pocket119
  BaseFeature = -> Pocket118
  Direction = (-1,0,0)
  Length = 5
  Length2 = 100
  Profile = -> Sketch285
  ReferenceAxis = -> Sketch285 [N_Axis]
  Suppressed = false
  Type = 1
FEATURE [Sketcher::SketchObject] Sketch286
  ArcFitTolerance = 1e-06
  AttachmentSupport = -> [Pocket119]
  ExternalGeometry = -> [Pocket119]
  FullyConstrained = true
  MakeInternals = false
  MapMode = 5
  Placement = pos=(50,0,0) rot=(0.57735,0.57735,0.57735;2.0944rad)
  sketch-geometry (4):
    g0: Circle CenterX=12 CenterY=17 CenterZ=0 NormalX=0 NormalY=0 NormalZ=1 AngleXU=0 Radius=2.125
    g1: Circle CenterX=28 CenterY=17 CenterZ=0 NormalX=0 NormalY=0 NormalZ=1 AngleXU=0 Radius=2.125
    g2: Circle CenterX=28 CenterY=3 CenterZ=0 NormalX=0 NormalY=0 NormalZ=1 AngleXU=0 Radius=2.125
    g3: Circle CenterX=12 CenterY=3 CenterZ=0 NormalX=0 NormalY=0 NormalZ=1 AngleXU=0 Radius=2.125
  constraints (8):
    c: Equal(g0,g1)
    c: Equal(g1,g3)
    c: Equal(g3,g2)
    c: Diameter(g0) = 4.25
    c: Coincident(g0,g-3)
    c: Coincident(g-4,g1)
    c: Coincident(g-5,g2)
    c: Coincident(g-6,g3)
FEATURE [PartDesign::Pocket] Pocket120
  BaseFeature = -> Pocket119
  Direction = (-1,0,0)
  Length = 1.5
  Length2 = 5
  Profile = -> Sketch286
  ReferenceAxis = -> Sketch286 [N_Axis]
  Refine = true
  Suppressed = false
  Type = 0
FEATURE [Sketcher::SketchObject] Sketch287
  ArcFitTolerance = 1e-06
  AttachmentSupport = -> [Pocket120]
  ExternalGeometry = -> [Pocket120]
  FullyConstrained = true
  MakeInternals = false
  MapMode = 5
  Placement = pos=(0,0,0) rot=(0.57735,-0.57735,-0.57735;2.0944rad)
  sketch-geometry (4):
    g0: Circle CenterX=-28 CenterY=17 CenterZ=0 NormalX=0 NormalY=0 NormalZ=1 AngleXU=0 Radius=2.1
    g1: Circle CenterX=-12 CenterY=17 CenterZ=0 NormalX=0 NormalY=0 NormalZ=1 AngleXU=0 Radius=2.1
    g2: Circle CenterX=-12 CenterY=3 CenterZ=0 NormalX=0 NormalY=0 NormalZ=1 AngleXU=0 Radius=2.1
    g3: Circle CenterX=-28 CenterY=3 CenterZ=0 NormalX=0 NormalY=0 NormalZ=1 AngleXU=0 Radius=2.1
  constraints (8):
    c: Equal(g0,g1)
    c: Equal(g1,g3)
    c: Equal(g3,g2)
    c: Diameter(g0) = 4.2
    c: Coincident(g0,g-3)
    c: Coincident(g-4,g1)
    c: Coincident(g-5,g2)
    c: Coincident(g3,g-6)
FEATURE [PartDesign::Pocket] Pocket121
  BaseFeature = -> Pocket120
  Direction = (1,0,0)
  Length = 1.5
  Length2 = 5
  Profile = -> Sketch287
  ReferenceAxis = -> Sketch287 [N_Axis]
  Refine = true
  Suppressed = false
  Type = 0
FEATURE [Sketcher::SketchObject] Sketch288
  ArcFitTolerance = 1e-06
  AttachmentSupport = -> [Pocket121]
  ExternalGeometry = -> [Pocket121]
  FullyConstrained = true
  MakeInternals = false
  MapMode = 5
  Placement = pos=(0,0,20) rot=(0,0,1;0rad)
  sketch-geometry (4):
    g0: Circle CenterX=4 CenterY=36 CenterZ=0 NormalX=0 NormalY=0 NormalZ=1 AngleXU=0 Radius=2.1
    g1: Circle CenterX=46 CenterY=36 CenterZ=0 NormalX=0 NormalY=0 NormalZ=1 AngleXU=0 Radius=2.1
    g2: Circle CenterX=4 CenterY=4 CenterZ=0 NormalX=0 NormalY=0 NormalZ=1 AngleXU=0 Radius=2.1
    g3: Circle CenterX=46 CenterY=4 CenterZ=0 NormalX=0 NormalY=0 NormalZ=1 AngleXU=0 Radius=2.1
  constraints (8):
    c: Coincident(g0,g-3)
    c: Coincident(g1,g-6)
    c: Coincident(g2,g-4)
    c: Coincident(g3,g-5)
    c: Equal(g0,g2)
    c: Equal(g2,g1)
    c: Equal(g1,g3)
    c: Diameter(g0) = 4.2
FEATURE [PartDesign::Pocket] Pocket122
  BaseFeature = -> Pocket121
  Direction = (0,0,-1)
  Length = 1.5
  Length2 = 5
  Profile = -> Sketch288
  ReferenceAxis = -> Sketch288 [N_Axis]
  Refine = true
  Suppressed = false
  Type = 0
FEATURE [Sketcher::SketchObject] Sketch289
  ArcFitTolerance = 1e-06
  AttachmentSupport = -> [Pocket122]
  ExternalGeometry = -> [Pocket122]
  FullyConstrained = true
  MakeInternals = false
  MapMode = 5
  Placement = pos=(0,0,-2) rot=(1,0,0;3.14159rad)
  sketch-geometry (4):
    g0: Circle CenterX=4 CenterY=-4 CenterZ=0 NormalX=0 NormalY=0 NormalZ=1 AngleXU=0 Radius=2.1
    g1: Circle CenterX=46 CenterY=-4 CenterZ=0 NormalX=0 NormalY=0 NormalZ=1 AngleXU=0 Radius=2.1
    g2: Circle CenterX=46 CenterY=-36 CenterZ=0 NormalX=0 NormalY=0 NormalZ=1 AngleXU=0 Radius=2.1
    g3: Circle CenterX=4 CenterY=-36 CenterZ=0 NormalX=0 NormalY=0 NormalZ=1 AngleXU=0 Radius=2.1
  constraints (8):
    c: Coincident(g0,g-3)
    c: Coincident(g1,g-5)
    c: Coincident(g2,g-6)
    c: Coincident(g3,g-4)
    c: Equal(g0,g1)
    c: Equal(g1,g2)
    c: Equal(g2,g3)
    c: Diameter(g0) = 4.2
FEATURE [PartDesign::Pocket] Pocket123
  BaseFeature = -> Pocket122
  Direction = (0,0,1)
  Length = 1.5
  Length2 = 5
  Profile = -> Sketch289
  ReferenceAxis = -> Sketch289 [N_Axis]
  Refine = true
  Suppressed = false
  Type = 0
FEATURE [PartDesign::Body] Body101  label="pince_support_servo002"
  AllowCompound = false
  Group = -> [Sketch282,Pad137,Sketch283,Pad138,Sketch284,Pocket118,Sketch285,Pocket119,Sketch286,Pocket120,Sketch287,Pocket121,Sketch288,Pocket122,Sketch289,Pocket123]
  Origin = -> Origin374
  Tip = -> Pocket123
COMPONENT P14 — recipe-attached ("pince_cremaillere_pignon002", modeled in this document).
Construction recipe (the document's own serialized feature program — sketch geometry with constraints, then the solid features built on it; lengths are millimeters unless a unit is written):

FEATURE [PartDesign::FeatureBase] BaseFeature005
  BaseFeature = -> InvoluteGear002
  Suppressed = false
FEATURE [Sketcher::SketchObject] Sketch290
  ArcFitTolerance = 0
  FullyConstrained = true
  MakeInternals = false
  MapMode = 5
  Placement = pos=(0,0,5.5) rot=(0,0,1;0rad)
  sketch-geometry (8):
    g0: Circle [constr] CenterX=0 CenterY=0 CenterZ=0 NormalX=0 NormalY=0 NormalZ=1 AngleXU=0 Radius=7
    g1: Circle CenterX=0 CenterY=7 CenterZ=0 NormalX=0 NormalY=0 NormalZ=1 AngleXU=0 Radius=1.65
    g2: Circle CenterX=-7 CenterY=0 CenterZ=0 NormalX=0 NormalY=0 NormalZ=1 AngleXU=0 Radius=1.65
    g3: Circle CenterX=7 CenterY=0 CenterZ=0 NormalX=0 NormalY=0 NormalZ=1 AngleXU=0 Radius=1.65
    g4: Circle CenterX=0 CenterY=-7 CenterZ=0 NormalX=0 NormalY=0 NormalZ=1 AngleXU=0 Radius=1.65
    g5: Circle CenterX=0 CenterY=0 CenterZ=0 NormalX=0 NormalY=0 NormalZ=1 AngleXU=0 Radius=3
    g6: LineSegment [constr] StartX=-7 StartY=0 StartZ=0 EndX=7 EndY=0 EndZ=0
    g7: LineSegment [constr] StartX=0 StartY=7 StartZ=0 EndX=0 EndY=-7 EndZ=0
  constraints (20):
    c: Coincident(g5,g0)
    c: Coincident(g5,g-1)
    c: PointOnObject(g2,g0)
    c: PointOnObject(g1,g0)
    c: PointOnObject(g3,g0)
    c: PointOnObject(g4,g0)
    c: Coincident(g2,g6)
    c: Coincident(g1,g7)
    c: Coincident(g6,g3)
    c: Coincident(g7,g4)
    c: PointOnObject(g5,g7)
    c: PointOnObject(g5,g6)
    c: Perpendicular(g7,g6)
    c: Equal(g1,g3)
    c: Equal(g1,g2)
    c: Equal(g1,g4)
    c: Diameter(g1) = 3.3
    c: Diameter(g5) = 6
    c: Diameter(g0) = 14
    c: PointOnObject(g2,g-1)
FEATURE [PartDesign::Pocket] Pocket124
  BaseFeature = -> BaseFeature005
  Direction = (0,0,-1)
  Length = 5
  Length2 = 100
  Profile = -> Sketch290
  Suppressed = false
  Type = 1
FEATURE [Sketcher::SketchObject] Sketch291
  ArcFitTolerance = 0
  AttachmentSupport = -> [Pocket124]
  ExternalGeometry = -> [Pocket124]
  FullyConstrained = true
  MakeInternals = false
  MapMode = 5
  Placement = pos=(0,0,0) rot=(1,0,0;3.14159rad)
  sketch-geometry (4):
    g0: Circle CenterX=0 CenterY=-7 CenterZ=0 NormalX=0 NormalY=0 NormalZ=1 AngleXU=0 Radius=3.25
    g1: Circle CenterX=-7 CenterY=0 CenterZ=0 NormalX=0 NormalY=0 NormalZ=1 AngleXU=0 Radius=3.25
    g2: Circle CenterX=7 CenterY=0 CenterZ=0 NormalX=0 NormalY=0 NormalZ=1 AngleXU=0 Radius=3.25
    g3: Circle CenterX=0 CenterY=7 CenterZ=0 NormalX=0 NormalY=0 NormalZ=1 AngleXU=0 Radius=3.25
  constraints (8):
    c: Coincident(g1,g-5)
    c: Coincident(g0,g-3)
    c: Coincident(g2,g-4)
    c: Coincident(g3,g-6)
    c: Equal(g2,g0)
    c: Equal(g2,g1)
    c: Equal(g2,g3)
    c: Diameter(g2) = 6.5
FEATURE [PartDesign::Pocket] Pocket125
  BaseFeature = -> Pocket124
  Direction = (0,0,1)
  Length = 3.5
  Length2 = 100
  Profile = -> Sketch291
  Suppressed = false
  Type = 0
FEATURE [PartDesign::Body] Body102  label="pince_cremaillere_pignon002"
  AllowCompound = false
  BaseFeature = -> InvoluteGear002
  Group = -> [BaseFeature005,Sketch290,Pocket124,Sketch291,Pocket125]
  Origin = -> Origin375
  Placement = pos=(25,20,27.098) rot=(0.715163,-0.698958,0;3.14159rad)
  Tip = -> Pocket125
COMPONENT P15 — recipe-attached ("pince_support_cremaillere002", modeled in this document).
Construction recipe (the document's own serialized feature program — sketch geometry with constraints, then the solid features built on it; lengths are millimeters unless a unit is written):

FEATURE [Sketcher::SketchObject] Sketch292
  ArcFitTolerance = 0
  FullyConstrained = true
  MakeInternals = false
  MapMode = 2
  sketch-geometry (25):
    g0: LineSegment StartX=0 StartY=50 StartZ=0 EndX=100 EndY=50 EndZ=0
    g1: LineSegment StartX=100 StartY=50 StartZ=0 EndX=100 EndY=0 EndZ=0
    g2: LineSegment StartX=100 StartY=0 StartZ=0 EndX=0 EndY=0 EndZ=0
    g3: LineSegment StartX=0 StartY=0 StartZ=0 EndX=0 EndY=50 EndZ=0
    g4: Circle CenterX=50 CenterY=25 CenterZ=0 NormalX=0 NormalY=0 NormalZ=1 AngleXU=0 Radius=14
    g5: LineSegment [constr] StartX=0 StartY=50 StartZ=0 EndX=100 EndY=0 EndZ=0
    g6: LineSegment [constr] StartX=0 StartY=0 StartZ=0 EndX=100 EndY=50 EndZ=0
    g7: LineSegment [constr] StartX=29 StartY=41 StartZ=0 EndX=71 EndY=41 EndZ=0
    g8: LineSegment [constr] StartX=71 StartY=41 StartZ=0 EndX=71 EndY=9 EndZ=0
    g9: LineSegment [constr] StartX=71 StartY=9 StartZ=0 EndX=29 EndY=9 EndZ=0
    g10: LineSegment [constr] StartX=29 StartY=9 StartZ=0 EndX=29 EndY=41 EndZ=0
    g11: Circle CenterX=29 CenterY=41 CenterZ=0 NormalX=0 NormalY=0 NormalZ=1 AngleXU=0 Radius=1.75
    g12: Circle CenterX=71 CenterY=41 CenterZ=0 NormalX=0 NormalY=0 NormalZ=1 AngleXU=0 Radius=1.75
    g13: Circle CenterX=71 CenterY=9 CenterZ=0 NormalX=0 NormalY=0 NormalZ=1 AngleXU=0 Radius=1.75
    g14: Circle CenterX=29 CenterY=9 CenterZ=0 NormalX=0 NormalY=0 NormalZ=1 AngleXU=0 Radius=1.75
    g15: LineSegment [constr] StartX=0 StartY=25 StartZ=0 EndX=100 EndY=25 EndZ=0
    g16: LineSegment [constr] StartX=50 StartY=50 StartZ=0 EndX=50 EndY=0 EndZ=0
    g17: LineSegment [constr] StartX=3.5 StartY=33.25 StartZ=0 EndX=96.5 EndY=33.25 EndZ=0
    g18: LineSegment [constr] StartX=96.5 StartY=33.25 StartZ=0 EndX=96.5 EndY=16.75 EndZ=0
    g19: LineSegment [constr] StartX=96.5 StartY=16.75 StartZ=0 EndX=3.5 EndY=16.75 EndZ=0
    g20: LineSegment [constr] StartX=3.5 StartY=16.75 StartZ=0 EndX=3.5 EndY=33.25 EndZ=0
    g21: Circle CenterX=96.5 CenterY=33.25 CenterZ=0 NormalX=0 NormalY=0 NormalZ=1 AngleXU=0 Radius=1.65
    g22: Circle CenterX=3.5 CenterY=33.25 CenterZ=0 NormalX=0 NormalY=0 NormalZ=1 AngleXU=0 Radius=1.65
    g23: Circle CenterX=3.5 CenterY=16.75 CenterZ=0 NormalX=0 NormalY=0 NormalZ=1 AngleXU=0 Radius=1.65
    g24: Circle CenterX=96.5 CenterY=16.75 CenterZ=0 NormalX=0 NormalY=0 NormalZ=1 AngleXU=0 Radius=1.65
  constraints (60):
    c: Coincident(g0,g1)
    c: Coincident(g1,g2)
    c: Coincident(g2,g3)
    c: Coincident(g3,g0)
    c: Horizontal(g0)
    c: Horizontal(g2)
    c: Vertical(g1)
    c: Vertical(g3)
    c: Coincident(g2,g-1)
    c: Coincident(g5,g0)
    c: Coincident(g2,g6)
    c: Coincident(g0,g6)
    c: Coincident(g1,g5)
    c: PointOnObject(g4,g6)
    c: PointOnObject(g4,g5)
    c: Diameter(g4) = 28
    c: DistanceY(g3,g3) = 50
    c: DistanceX(g2,g2) = 100
    c: Coincident(g7,g8)
    c: Coincident(g8,g9)
    c: Coincident(g9,g10)
    c: Coincident(g10,g7)
    c: Horizontal(g7)
    c: Vertical(g10)
    c: Coincident(g11,g7)
    c: Coincident(g7,g12)
    c: Coincident(g9,g14)
    c: Coincident(g8,g13)
    c: Equal(g11,g12)
    c: Equal(g11,g14)
    c: Equal(g11,g13)
    c: Radius(g11) = 1.75
    c: DistanceY(g10,g10) = 32
    c: DistanceX(g7,g7) = 42
    c: PointOnObject(g16,g0)
    c: PointOnObject(g15,g1)
    c: PointOnObject(g15,g3)
    c: PointOnObject(g16,g2)
    c: Symmetric(g0,g0,g16)
    c: Symmetric(g0,g2,g15)
    c: Symmetric(g14,g13,g16)
    c: Symmetric(g12,g13,g15)
    c: Coincident(g17,g18)
    c: Coincident(g18,g19)
    c: Coincident(g19,g20)
    c: Coincident(g20,g17)
    c: Horizontal(g19)
    c: Vertical(g20)
    c: Symmetric(g17,g18,g15)
    c: Symmetric(g17,g17,g16)
    c: Distance(g20) = 16.5
    c: DistanceX(g0,g17) = 3.5
    c: Coincident(g24,g18)
    c: Coincident(g21,g17)
    c: Coincident(g17,g22)
    c: Coincident(g19,g23)
    c: Equal(g22,g23)
    c: Equal(g22,g21)
    c: Equal(g22,g24)
    c: Diameter(g22) = 3.3
FEATURE [PartDesign::Pad] Pad139
  AlongSketchNormal = false
  Direction = (0,0,1)
  Length = 8
  Length2 = 100
  Profile = -> Sketch292
  Suppressed = false
  Type = 0
FEATURE [Sketcher::SketchObject] Sketch293
  ArcFitTolerance = 0
  AttachmentSupport = -> [Pad139]
  ExternalGeometry = -> [Pad139]
  FullyConstrained = true
  MakeInternals = false
  MapMode = 5
  Placement = pos=(0,0,8) rot=(0,0,1;0rad)
  sketch-geometry (9):
    g0: LineSegment StartX=0 StartY=48 StartZ=0 EndX=100 EndY=48 EndZ=0
    g1: LineSegment StartX=100 StartY=48 StartZ=0 EndX=100 EndY=35.75 EndZ=0
    g2: LineSegment StartX=100 StartY=35.75 StartZ=0 EndX=0 EndY=35.75 EndZ=0
    g3: LineSegment StartX=0 StartY=35.75 StartZ=0 EndX=0 EndY=48 EndZ=0
    g4: LineSegment StartX=0 StartY=2 StartZ=0 EndX=100 EndY=2 EndZ=0
    g5: LineSegment StartX=100 StartY=2 StartZ=0 EndX=100 EndY=14.25 EndZ=0
    g6: LineSegment StartX=100 StartY=14.25 StartZ=0 EndX=0 EndY=14.25 EndZ=0
    g7: LineSegment StartX=0 StartY=14.25 StartZ=0 EndX=0 EndY=2 EndZ=0
    g8: Circle [constr] CenterX=50 CenterY=25 CenterZ=0 NormalX=0 NormalY=0 NormalZ=1 AngleXU=0 Radius=10.75
  constraints (26):
    c: Coincident(g0,g1)
    c: Coincident(g1,g2)
    c: Coincident(g2,g3)
    c: Coincident(g3,g0)
    c: Horizontal(g0)
    c: Horizontal(g2)
    c: Vertical(g1)
    c: Vertical(g3)
    c: Coincident(g4,g5)
    c: Coincident(g5,g6)
    c: Coincident(g6,g7)
    c: Coincident(g7,g4)
    c: Horizontal(g4)
    c: Horizontal(g6)
    c: Vertical(g5)
    c: Vertical(g7)
    c: PointOnObject(g6,g-6)
    c: PointOnObject(g2,g-6)
    c: PointOnObject(g1,g-5)
    c: PointOnObject(g5,g-5)
    c: Coincident(g8,g-7)
    c: Diameter(g8) = 21.5
    c: Tangent(g8,g2)
    c: Tangent(g6,g8)
    c: Equal(g7,g3)
    c: DistanceY(g0,g-6) = 2
FEATURE [PartDesign::Pocket] Pocket126
  BaseFeature = -> Pad139
  Direction = (0,0,-1)
  Length = 4
  Length2 = 100
  Profile = -> Sketch293
  Suppressed = false
  Type = 0
FEATURE [Sketcher::SketchObject] Sketch294
  ArcFitTolerance = 0
  AttachmentSupport = -> [Pocket126]
  ExternalGeometry = -> [Pocket126]
  FullyConstrained = true
  MakeInternals = false
  MapMode = 5
  Placement = pos=(0,0,8) rot=(0,0,1;0rad)
  sketch-geometry (10):
    g0: ArcOfCircle CenterX=11 CenterY=25 CenterZ=0 NormalX=0 NormalY=0 NormalZ=1 AngleXU=0 Radius=8 StartAngle=1.5708 EndAngle=4.71239
    g1: ArcOfCircle CenterX=26 CenterY=25 CenterZ=0 NormalX=0 NormalY=0 NormalZ=1 AngleXU=0 Radius=8 StartAngle=4.71239 EndAngle=7.85398
    g2: LineSegment StartX=11 StartY=17 StartZ=0 EndX=26 EndY=17 EndZ=0
    g3: LineSegment StartX=26 StartY=33 StartZ=0 EndX=11 EndY=33 EndZ=0
    g4: ArcOfCircle CenterX=74 CenterY=25 CenterZ=0 NormalX=0 NormalY=0 NormalZ=1 AngleXU=0 Radius=8 StartAngle=1.5708 EndAngle=4.71239
    g5: ArcOfCircle CenterX=89 CenterY=25 CenterZ=0 NormalX=0 NormalY=0 NormalZ=1 AngleXU=0 Radius=8 StartAngle=4.71239 EndAngle=7.85398
    g6: LineSegment StartX=74 StartY=17 StartZ=0 EndX=89 EndY=17 EndZ=0
    g7: LineSegment StartX=89 StartY=33 StartZ=0 EndX=74 EndY=33 EndZ=0
    g8: LineSegment [constr] StartX=50 StartY=50 StartZ=0 EndX=50 EndY=0 EndZ=0
    g9: LineSegment [constr] StartX=0 StartY=25 StartZ=0 EndX=100 EndY=25 EndZ=0
  constraints (26):
    c: Tangent(g0,g2) = -1.5708
    c: Tangent(g2,g1) = -1.5708
    c: Tangent(g1,g3) = -1.5708
    c: Tangent(g3,g0) = -1.5708
    c: Equal(g0,g1)
    c: Tangent(g4,g6) = -1.5708
    c: Tangent(g6,g5) = -1.5708
    c: Tangent(g5,g7) = -1.5708
    c: Tangent(g7,g4) = -1.5708
    c: Equal(g4,g5)
    c: PointOnObject(g-7,g9)
    c: PointOnObject(g-7,g8)
    c: PointOnObject(g8,g-6)
    c: PointOnObject(g8,g-5)
    c: PointOnObject(g9,g-3)
    c: PointOnObject(g9,g-4)
    c: Horizontal(g9)
    c: Vertical(g8)
    c: PointOnObject(g0,g9)
    c: PointOnObject(g1,g9)
    c: Symmetric(g1,g4,g8)
    c: Symmetric(g5,g0,g8)
    c: Equal(g1,g4)
    c: DistanceX(g-3,g0) = 11
    c: DistanceX(g1,g8) = 24
    c: DistanceY(g-7,g1) = 8
FEATURE [PartDesign::Pocket] Pocket127
  BaseFeature = -> Pocket126
  Direction = (0,0,-1)
  Length = 5
  Length2 = 100
  Profile = -> Sketch294
  Suppressed = false
  Type = 1
FEATURE [Sketcher::SketchObject] Sketch295
  ArcFitTolerance = 0
  AttachmentSupport = -> [Pocket127]
  ExternalGeometry = -> [Pocket127]
  FullyConstrained = true
  MakeInternals = false
  MapMode = 5
  Placement = pos=(0,0,4) rot=(0,0,1;0rad)
  sketch-geometry (4):
    g0: Circle CenterX=29 CenterY=41 CenterZ=0 NormalX=0 NormalY=0 NormalZ=1 AngleXU=0 Radius=3.5
    g1: Circle CenterX=71 CenterY=41 CenterZ=0 NormalX=0 NormalY=0 NormalZ=1 AngleXU=0 Radius=3.5
    g2: Circle CenterX=29 CenterY=9 CenterZ=0 NormalX=0 NormalY=0 NormalZ=1 AngleXU=0 Radius=3.5
    g3: Circle CenterX=71 CenterY=9 CenterZ=0 NormalX=0 NormalY=0 NormalZ=1 AngleXU=0 Radius=3.5
  constraints (8):
    c: Coincident(g-3,g0)
    c: Coincident(g1,g-4)
    c: Coincident(g2,g-5)
    c: Coincident(g3,g-6)
    c: Equal(g0,g1)
    c: Equal(g0,g2)
    c: Equal(g0,g3)
    c: Diameter(g0) = 7
FEATURE [PartDesign::Pocket] Pocket128
  BaseFeature = -> Pocket127
  Direction = (0,0,-1)
  Length = 2
  Length2 = 100
  Profile = -> Sketch295
  Suppressed = false
  Type = 0
FEATURE [PartDesign::Body] Body103  label="pince_support_cremaillere002"
  AllowCompound = false
  Group = -> [Sketch292,Pad139,Sketch293,Pocket126,Sketch294,Pocket127,Sketch295,Pocket128]
  Origin = -> Origin376
  Placement = pos=(-25,-5,20) rot=(0,0,1;0rad)
  Tip = -> Pocket128
COMPONENT P16 — recipe-attached ("mousse004", modeled in this document).
Construction recipe (the document's own serialized feature program — sketch geometry with constraints, then the solid features built on it; lengths are millimeters unless a unit is written):

FEATURE [Sketcher::SketchObject] Sketch296
  ArcFitTolerance = 1e-06
  AttachmentSupport = -> [XZ_Plane374]
  FullyConstrained = true
  MakeInternals = false
  MapMode = 5
  Placement = pos=(0,0,0) rot=(1,0,0;1.5708rad)
  sketch-geometry (4):
    g0: LineSegment StartX=-4.5 StartY=0 StartZ=0 EndX=4.5 EndY=0 EndZ=0
    g1: LineSegment StartX=4.5 StartY=0 StartZ=0 EndX=4.5 EndY=3 EndZ=0
    g2: LineSegment StartX=4.5 StartY=3 StartZ=0 EndX=-4.5 EndY=3 EndZ=0
    g3: LineSegment StartX=-4.5 StartY=3 StartZ=0 EndX=-4.5 EndY=0 EndZ=0
  constraints (11):
    c: Coincident(g0,g1)
    c: Coincident(g1,g2)
    c: Coincident(g2,g3)
    c: Coincident(g3,g0)
    c: Horizontal(g0)
    c: Vertical(g1)
    c: Vertical(g3)
    c: PointOnObject(g0,g-1)
    c: Symmetric(g1,g2,g-2)
    c: Distance(g2,g2) = 9
    c: DistanceY(g3,g3) = 3
FEATURE [PartDesign::Pad] Pad140
  Direction = (0,-1,2e-16)
  Length = 40
  Length2 = 10
  Midplane = true
  Placement = pos=(0,0,0) rot=(1,0,0;1.5708rad)
  Profile = -> Sketch296
  ReferenceAxis = -> Sketch296 [N_Axis]
  Suppressed = false
  Type = 0
FEATURE [PartDesign::Body] Body104  label="mousse004"
  AllowCompound = false
  Group = -> [Sketch296,Pad140]
  Origin = -> Origin377
  Placement = pos=(71.5056,23,59.5) rot=(0.707107,0,0.707107;3.14159rad)
  Tip = -> Pad140
COMPONENT P17 — recipe-attached ("cale001", modeled in this document).
Construction recipe (the document's own serialized feature program — sketch geometry with constraints, then the solid features built on it; lengths are millimeters unless a unit is written):

FEATURE [Sketcher::SketchObject] Sketch300
  ArcFitTolerance = 1e-06
  AttachmentSupport = -> [XZ_Plane377]
  FullyConstrained = true
  MakeInternals = false
  MapMode = 5
  Placement = pos=(0,0,0) rot=(1,0,0;1.5708rad)
  sketch-geometry (4):
    g0: LineSegment StartX=-4.5 StartY=0 StartZ=0 EndX=4.5 EndY=0 EndZ=0
    g1: LineSegment StartX=4.5 StartY=0 StartZ=0 EndX=4.5 EndY=2 EndZ=0
    g2: LineSegment StartX=4.5 StartY=2 StartZ=0 EndX=-4.5 EndY=2 EndZ=0
    g3: LineSegment StartX=-4.5 StartY=2 StartZ=0 EndX=-4.5 EndY=0 EndZ=0
  constraints (11):
    c: Coincident(g0,g1)
    c: Coincident(g1,g2)
    c: Coincident(g2,g3)
    c: Coincident(g3,g0)
    c: Horizontal(g0)
    c: Vertical(g1)
    c: Vertical(g3)
    c: PointOnObject(g0,g-1)
    c: Symmetric(g1,g2,g-2)
    c: Distance(g2,g2) = 9
    c: DistanceY(g3,g3) = 2
FEATURE [PartDesign::Pad] Pad142
  Direction = (0,-1,2e-16)
  Length = 40
  Length2 = 10
  Midplane = true
  Placement = pos=(0,0,0) rot=(1,0,0;1.5708rad)
  Profile = -> Sketch300
  ReferenceAxis = -> Sketch300 [N_Axis]
  Suppressed = false
  Type = 0
FEATURE [PartDesign::Body] Body105  label="cale001"
  AllowCompound = false
  Group = -> [Sketch300,Pad142]
  Origin = -> Origin380
  Placement = pos=(71.5056,23,59.5) rot=(0.707107,0,0.707107;3.14159rad)
  Tip = -> Pad142
COMPONENT P18 — recipe-attached ("jonction_rail_pince001", modeled in this document).
Construction recipe (the document's own serialized feature program — sketch geometry with constraints, then the solid features built on it; lengths are millimeters unless a unit is written):

FEATURE [Sketcher::SketchObject] Sketch305
  ArcFitTolerance = 1e-06
  AttachmentSupport = -> [YZ_Plane378]
  FullyConstrained = true
  MakeInternals = false
  MapMode = 5
  Placement = pos=(0,0,0) rot=(0.57735,0.57735,0.57735;2.0944rad)
  sketch-geometry (8):
    g0: LineSegment StartX=-11 StartY=10 StartZ=0 EndX=-11 EndY=-10 EndZ=0
    g1: LineSegment StartX=-11 StartY=-10 StartZ=0 EndX=11 EndY=-10 EndZ=0
    g2: LineSegment StartX=11 StartY=-10 StartZ=0 EndX=11 EndY=10 EndZ=0
    g3: LineSegment StartX=11 StartY=10 StartZ=0 EndX=-11 EndY=10 EndZ=0
    g4: Circle CenterX=8 CenterY=-7 CenterZ=0 NormalX=0 NormalY=0 NormalZ=1 AngleXU=0 Radius=1.75
    g5: Circle CenterX=-8 CenterY=-7 CenterZ=0 NormalX=0 NormalY=0 NormalZ=1 AngleXU=0 Radius=1.75
    g6: Circle CenterX=8 CenterY=7 CenterZ=0 NormalX=0 NormalY=0 NormalZ=1 AngleXU=0 Radius=1.75
    g7: Circle CenterX=-8 CenterY=7 CenterZ=0 NormalX=0 NormalY=0 NormalZ=1 AngleXU=0 Radius=1.75
  constraints (21):
    c: Coincident(g0,g1)
    c: Coincident(g1,g2)
    c: Coincident(g2,g3)
    c: Coincident(g3,g0)
    c: Vertical(g0)
    c: Vertical(g2)
    c: Horizontal(g1)
    c: Distance(g1,g1) = 22
    c: Symmetric(g0,g1,g-1)
    c: Horizontal(g3)
    c: DistanceY(g2,g2) = 20
    c: Diameter(g4) = 3.5
    c: Diameter(g5) = 3.5
    c: Diameter(g6) = 3.5
    c: Diameter(g7) = 3.5
    c: Symmetric(g7,g4,g-1)
    c: Symmetric(g5,g6,g-1)
    c: Horizontal(g6,g7)
    c: Vertical(g7,g5)
    c: DistanceX(g7,g-1) = 8
    c: DistanceY(g-1,g7) = 7
FEATURE [PartDesign::Pad] Pad144
  Direction = (1,0,0)
  Length = 5
  Length2 = 10
  Placement = pos=(0,0,0) rot=(1,1,1;2.0944rad)
  Profile = -> Sketch305
  ReferenceAxis = -> Sketch305 [N_Axis]
  Suppressed = false
  Type = 0
FEATURE [Sketcher::SketchObject] Sketch306
  ArcFitTolerance = 1e-06
  AttachmentOffset = pos=(0,0,5) rot=(0,0,1;0rad)
  AttachmentSupport = -> [YZ_Plane378]
  FullyConstrained = false
  MakeInternals = false
  MapMode = 5
  Placement = pos=(5,0,0) rot=(0.57735,0.57735,0.57735;2.0944rad)
  sketch-geometry (12):
    g0: LineSegment StartX=-3.23224 StartY=10 StartZ=0 EndX=-3.23224 EndY=3.23224 EndZ=0
    g1: LineSegment StartX=-3.23224 StartY=-10 StartZ=0 EndX=3.23224 EndY=-10 EndZ=0
    g2: LineSegment StartX=3.23224 StartY=-10 StartZ=0 EndX=3.23224 EndY=-3.23224 EndZ=0
    g3: LineSegment StartX=3.23224 StartY=10 StartZ=0 EndX=-3.23224 EndY=10 EndZ=0
    g4: LineSegment StartX=-11 StartY=-3.23224 StartZ=0 EndX=-3.23224 EndY=-3.23224 EndZ=0
    g5: LineSegment StartX=11 StartY=-3.23224 StartZ=0 EndX=11 EndY=3.23224 EndZ=0
    g6: LineSegment StartX=11 StartY=3.23224 StartZ=0 EndX=3.23224 EndY=3.23224 EndZ=0
    g7: LineSegment StartX=-11 StartY=3.23224 StartZ=0 EndX=-11 EndY=-3.23224 EndZ=0
    g8: LineSegment StartX=3.23224 StartY=3.23224 StartZ=0 EndX=3.23224 EndY=10 EndZ=0
    g9: LineSegment StartX=-3.23224 StartY=-3.23224 StartZ=0 EndX=-3.23224 EndY=-10 EndZ=0
    g10: LineSegment StartX=-3.23224 StartY=3.23224 StartZ=0 EndX=-11 EndY=3.23224 EndZ=0
    g11: LineSegment StartX=3.23224 StartY=-3.23224 StartZ=0 EndX=11 EndY=-3.23224 EndZ=0
  constraints (36):
    c: Coincident(g9,g1)
    c: Coincident(g1,g2)
    c: Coincident(g8,g3)
    c: Coincident(g3,g0)
    c: Vertical(g0)
    c: Vertical(g2)
    c: Horizontal(g1)
    c: Horizontal(g3)
    c: Coincident(g11,g5)
    c: Coincident(g5,g6)
    c: Coincident(g10,g7)
    c: Coincident(g7,g4)
    c: Horizontal(g4)
    c: Horizontal(g6)
    c: Vertical(g5)
    c: Vertical(g7)
    c: PointOnObject(g2,g11)
    c: PointOnObject(g0,g10)
    c: Coincident(g6,g8)
    c: PointOnObject(g10,g0)
    c: Coincident(g4,g9)
    c: PointOnObject(g11,g2)
    c: Equal(g0,g8)
    c: Equal(g2,g9)
    c: Equal(g7,g5)
    c: Equal(g5,g3)
    c: Equal(g3,g1)
    c: Symmetric(g2,g0,g-1)
    c: Horizontal(g10)
    c: Vertical(g9)
    c: Vertical(g4,g0)
    c: Vertical(g8)
    c: DistanceY(g-1,g0) = 10
    c: Equal(g10,g6)
    c: DistanceX(g7,g-1) = 11
    c: Equal(g2,g8)
FEATURE [PartDesign::Pad] Pad145
  BaseFeature = -> Pad144
  Direction = (1,0,0)
  Length = 100
  Length2 = 10
  Placement = pos=(0,0,0) rot=(1,1,1;2.0944rad)
  Profile = -> Sketch306
  ReferenceAxis = -> Sketch306 [N_Axis]
  Suppressed = false
  Type = 0
FEATURE [Sketcher::SketchObject] Sketch307
  ArcFitTolerance = 1e-06
  AttachmentSupport = -> [Pad145]
  FullyConstrained = true
  MakeInternals = false
  MapMode = 5
  Placement = pos=(105,0,0) rot=(0.57735,0.57735,0.57735;2.0944rad)
  sketch-geometry (2):
    g0: Circle CenterX=0 CenterY=5 CenterZ=0 NormalX=0 NormalY=0 NormalZ=1 AngleXU=0 Radius=2
    g1: Circle CenterX=0 CenterY=-5 CenterZ=0 NormalX=0 NormalY=0 NormalZ=1 AngleXU=0 Radius=2
  constraints (5):
    c: PointOnObject(g0,g-2)
    c: Symmetric(g0,g1,g-1)
    c: Equal(g1,g0)
    c: DistanceY(g1,g0) = 10
    c: Diameter(g0) = 4
FEATURE [PartDesign::Pocket] Pocket130
  BaseFeature = -> Pad145
  Direction = (-1,0,0)
  Length = 5
  Length2 = 5
  Placement = pos=(0,0,0) rot=(1,1,1;2.0944rad)
  Profile = -> Sketch307
  ReferenceAxis = -> Sketch307 [N_Axis]
  Suppressed = false
  Type = 0
FEATURE [PartDesign::Body] Body106  label="jonction_rail_pince001"
  AllowCompound = false
  Group = -> [Sketch305,Pad144,Sketch306,Pad145,Sketch307,Pocket130]
  Origin = -> Origin381
  Placement = pos=(-24.5372,-138.932,55.6643) rot=(0.004162,0.999972,-0.006227;3.15418rad)
  Tip = -> Pocket130
COMPONENT P19 — geometry summary ("L16_50MM_SW_ASM"; no construction recipe available for this part):
  bounding box: 176.4 x 26.1 x 20.0 mm
  tessellated surface: 37,470 triangles
  volume: 16350 mm^3 (18% of its bounding box)
COMPONENT P20 — same part as P18; its construction recipe is shown at P18.
COMPONENT P21 — same part as P3; its construction recipe is shown at P3.
COMPONENT P22 — same part as P7; its construction recipe is shown at P7.
COMPONENT P23 — same part as P12; its construction recipe is shown at P12.
COMPONENT P24 — same part as P16; its construction recipe is shown at P16.
